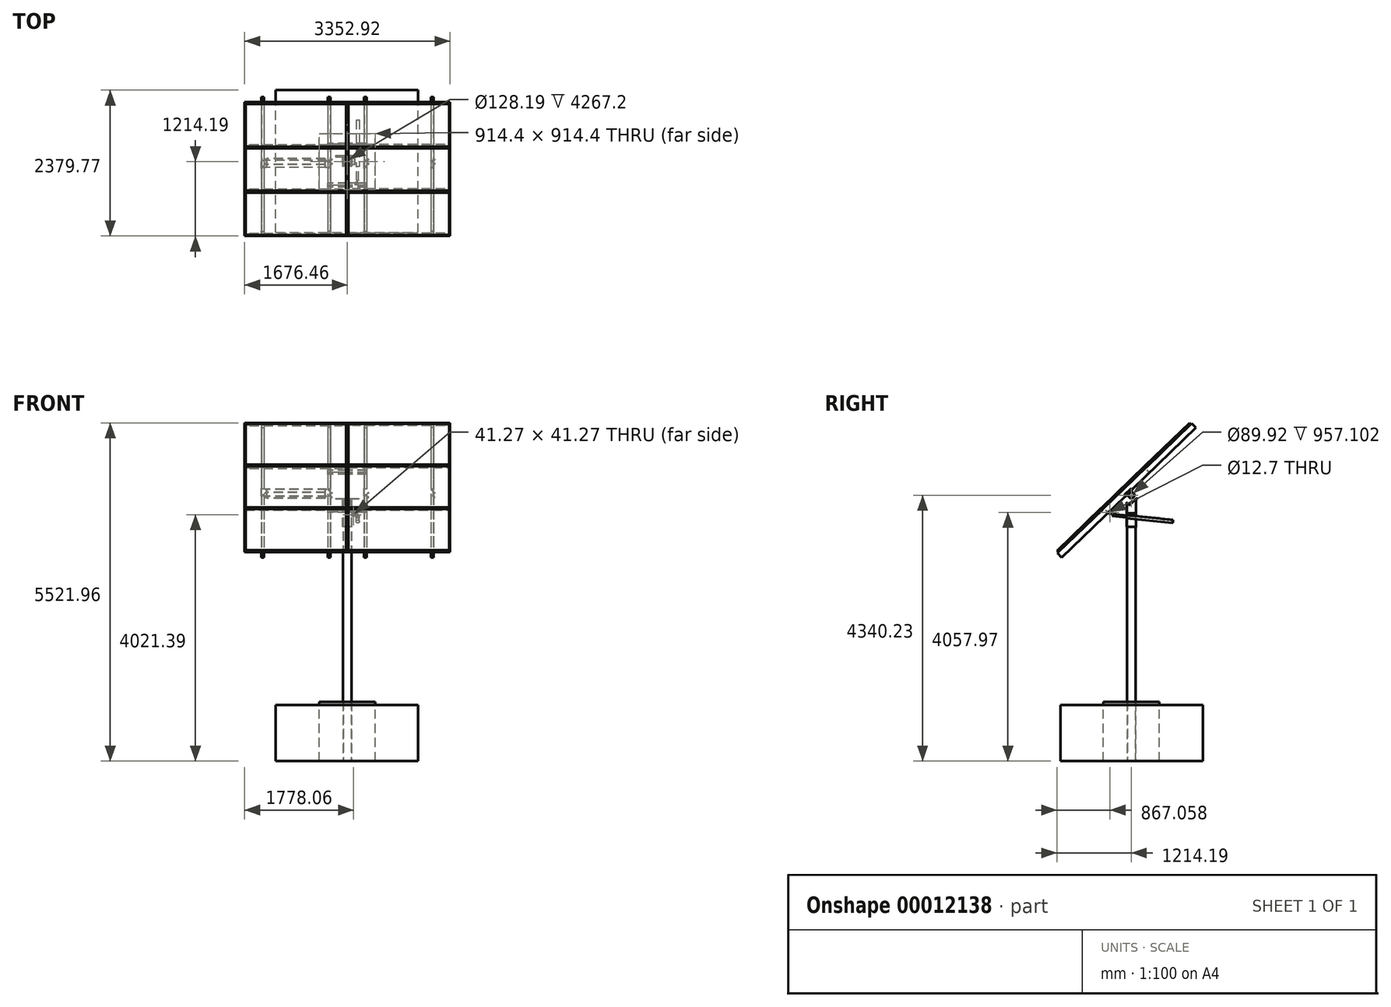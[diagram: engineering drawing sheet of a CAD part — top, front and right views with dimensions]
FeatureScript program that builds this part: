
annotation { "Feature Type Name" : "Feature", "Feature Type Description" : "" }
export const myFeature = defineFeature(function(context is Context, id is Id, definition is map)
    precondition{}
    {
        {
            var Q0;
            Q0=qCreatedBy(makeId("Top.planeOp"),FACE);
            var sketch = newSketch(context, id + "F0", { "sketchPlane" : qUnion([Q0])});
            skCircle(sketch, "E0", {"center": v(0, 0) * mm, "radius": 64.1 * mm});
            skCircle(sketch, "E1", {"center": v(0, 0) * mm, "radius": 70.65 * mm});
            skCircle(sketch, "E2", {"center": v(0, 0) * mm, "radius": 457.2 * mm, "construction": true});
            skLineSegment(sketch, "E3.bottom", {"start": v(-1167.5, -1157.81) * mm, "end": v(1155.89, -1157.81) * mm});
            skLineSegment(sketch, "E3.top", {"start": v(-1167.5, 1165.58) * mm, "end": v(1155.89, 1165.58) * mm});
            skLineSegment(sketch, "E3.left", {"start": v(-1167.5, -1157.81) * mm, "end": v(-1167.5, 1165.58) * mm});
            skLineSegment(sketch, "E3.right", {"start": v(1155.89, -1157.81) * mm, "end": v(1155.89, 1165.58) * mm});
            skLineSegment(sketch, "E4", {"start": v(0, 1165.58) * mm, "end": v(0, -1157.81) * mm, "construction": true});
            skLineSegment(sketch, "E5", {"start": v(-1167.5, 0) * mm, "end": v(1155.89, 0) * mm, "construction": true});
            skLineSegment(sketch, "E6.bottom", {"start": v(-457.2, -457.2) * mm, "end": v(457.2, -457.2) * mm});
            skLineSegment(sketch, "E6.top", {"start": v(-457.2, 457.2) * mm, "end": v(457.2, 457.2) * mm});
            skLineSegment(sketch, "E6.left", {"start": v(-457.2, -457.2) * mm, "end": v(-457.2, 457.2) * mm});
            skLineSegment(sketch, "E6.right", {"start": v(457.2, -457.2) * mm, "end": v(457.2, 457.2) * mm});
            skSolve(sketch);
        }
        {
            var Q0;
            Q0=makeQuery(id+"F0.imprint","IMPRINT",FACE,{"disambiguationData":[TD([[makeQuery(id+"F0.imprint","IMPRINT",EDGE,{"derivedFrom":sQuery(id+"F0.wireOp",EDGE,"E1")}),-1.0]])]});
            var Q1;
            Q1=makeQuery(id+"F0.imprint","IMPRINT",FACE,{"disambiguationData":[TD([[makeQuery(id+"F0.imprint","IMPRINT",EDGE,{"derivedFrom":sQuery(id+"F0.wireOp",EDGE,"E0")}),1.0]])]});
            var Q2;
            Q2=makeQuery(id+"F0.imprint","IMPRINT",FACE,{"disambiguationData":[TD([[makeQuery(id+"F0.imprint","IMPRINT",EDGE,{"derivedFrom":sQuery(id+"F0.wireOp",EDGE,"E0")}),-1.0]])]});
            extrude(context, id + "F1", {"entities" : qUnion([Q0, Q1, Q2]), "oppositeDirection" : true, "depth" : 914.4 * mm, "hasSecondDirection" : true, "secondDirectionOppositeDirection" : false, "secondDirectionDepth" : 50.8 * mm});
        }
        {
            var Q0;
            Q0=makeQuery(id+"F0.imprint","IMPRINT",FACE,{"disambiguationData":[TD([[makeQuery(id+"F0.imprint","IMPRINT",EDGE,{"derivedFrom":sQuery(id+"F0.wireOp",EDGE,"E0")}),-1.0]])]});
            extrude(context, id + "F2", {"entities" : qUnion([Q0]), "depth" : 3352.8 * mm, "hasSecondDirection" : true, "secondDirectionOppositeDirection" : true, "secondDirectionDepth" : 914.4 * mm});
        }
        {
            var Q0;
            Q0=makeQuery(id+"F0.imprint","IMPRINT",FACE,{"disambiguationData":[TD([[makeQuery(id+"F0.imprint","IMPRINT",EDGE,{"derivedFrom":sQuery(id+"F0.wireOp",EDGE,"E3.bottom")}),1.0]])]});
            extrude(context, id + "F3", {"entities" : qUnion([Q0]), "oppositeDirection" : true, "depth" : 914.4 * mm});
        }
        {
            var Q0;
            Q0=makeQuery(id+"F2.opExtrude","CAP_FACE",FACE,{"disambiguationData":[OSD([sQuery(id+"F0.wireOp",EDGE,"E0"),sQuery(id+"F0.wireOp",EDGE,"E1")])],"isStart":false});
            var sketch = newSketch(context, id + "F4", { "sketchPlane" : qUnion([Q0])});
            skCircle(sketch, "E7.0", {"center": v(0, 0) * mm, "radius": 70.65 * mm});
            skCircle(sketch, "E8", {"center": v(0, 49.5) * mm, "radius": 12.7 * mm});
            skCircle(sketch, "E9", {"center": v(0, 49.5) * mm, "radius": 6.35 * mm});
            skCircle(sketch, "E10", {"center": v(0, 49.5) * mm, "radius": 14.6 * mm, "construction": true});
            skLineSegment(sketch, "E11", {"start": v(0, 49.5) * mm, "end": v(0, 0) * mm, "construction": true});
            skCircle(sketch, "E12.1.0", {"center": v(-42.86, -24.75) * mm, "radius": 12.7 * mm});
            skCircle(sketch, "E12.1.1", {"center": v(-42.86, -24.75) * mm, "radius": 6.35 * mm});
            skCircle(sketch, "E12.2.0", {"center": v(42.86, -24.75) * mm, "radius": 12.7 * mm});
            skCircle(sketch, "E12.2.1", {"center": v(42.86, -24.75) * mm, "radius": 6.35 * mm});
            skSolve(sketch);
        }
        {
            var Q0;
            Q0 = qSketchRegion(id + "F4", true);
            var Q1;
            Q1=makeQuery(id+"F4.imprint","IMPRINT",FACE,{"disambiguationData":[TD([[makeQuery(id+"F4.imprint","IMPRINT",EDGE,{"derivedFrom":sQuery(id+"F4.wireOp",EDGE,"E8")}),1.0]])]});
            var Q2;
            Q2=makeQuery(id+"F4.imprint","IMPRINT",FACE,{"disambiguationData":[TD([[makeQuery(id+"F4.imprint","IMPRINT",EDGE,{"derivedFrom":sQuery(id+"F4.wireOp",EDGE,"E9")}),1.0]])]});
            var Q3;
            Q3=makeQuery(id+"F4.imprint","IMPRINT",FACE,{"disambiguationData":[TD([[makeQuery(id+"F4.imprint","IMPRINT",EDGE,{"derivedFrom":sQuery(id+"F4.wireOp",EDGE,"E12.1.0")}),1.0]])]});
            var Q4;
            Q4=makeQuery(id+"F4.imprint","IMPRINT",FACE,{"disambiguationData":[TD([[makeQuery(id+"F4.imprint","IMPRINT",EDGE,{"derivedFrom":sQuery(id+"F4.wireOp",EDGE,"E12.1.1")}),1.0]])]});
            var Q5;
            Q5=makeQuery(id+"F4.imprint","IMPRINT",FACE,{"disambiguationData":[TD([[makeQuery(id+"F4.imprint","IMPRINT",EDGE,{"derivedFrom":sQuery(id+"F4.wireOp",EDGE,"E12.2.1")}),1.0]])]});
            var Q6;
            Q6=makeQuery(id+"F4.imprint","IMPRINT",FACE,{"disambiguationData":[TD([[makeQuery(id+"F4.imprint","IMPRINT",EDGE,{"derivedFrom":sQuery(id+"F4.wireOp",EDGE,"E12.2.0")}),1.0]])]});
            extrude(context, id + "F5", {"entities" : qUnion([Q0, Q1, Q2, Q3, Q4, Q5, Q6]), "depth" : 6.35 * mm});
        }
        {
            var Q0;
            Q0=makeQuery(id+"F4.imprint","IMPRINT",FACE,{"disambiguationData":[TD([[makeQuery(id+"F4.imprint","IMPRINT",EDGE,{"derivedFrom":sQuery(id+"F4.wireOp",EDGE,"E8")}),1.0]])]});
            var Q1;
            Q1=makeQuery(id+"F4.imprint","IMPRINT",FACE,{"disambiguationData":[TD([[makeQuery(id+"F4.imprint","IMPRINT",EDGE,{"derivedFrom":sQuery(id+"F4.wireOp",EDGE,"E12.1.0")}),1.0]])]});
            var Q2;
            Q2=makeQuery(id+"F4.imprint","IMPRINT",FACE,{"disambiguationData":[TD([[makeQuery(id+"F4.imprint","IMPRINT",EDGE,{"derivedFrom":sQuery(id+"F4.wireOp",EDGE,"E12.2.0")}),1.0]])]});
            extrude(context, id + "F6", {"entities" : qUnion([Q0, Q1, Q2]), "oppositeDirection" : true, "depth" : 3.8 * mm});
        }
        {
            var Q0;
            Q0=makeQuery(id+"F5.opExtrude","CAP_FACE",FACE,{"disambiguationData":[OSD([sQuery(id+"F4.wireOp",EDGE,"E7.0")])],"isStart":false});
            var sketch = newSketch(context, id + "F7", { "sketchPlane" : qUnion([Q0])});
            skCircle(sketch, "E13", {"center": v(0, 0) * mm, "radius": 67.48 * mm});
            skCircle(sketch, "E14.0", {"center": v(0, 0) * mm, "radius": 70.65 * mm, "construction": true});
            skSolve(sketch);
        }
        {
            var Q0;
            Q0=makeQuery(id+"F7.imprint","IMPRINT",FACE,{"disambiguationData":[TD([[makeQuery(id+"F7.imprint","IMPRINT",EDGE,{"derivedFrom":sQuery(id+"F7.wireOp",EDGE,"E13")}),1.0]])]});
            extrude(context, id + "F8", {"entities" : qUnion([Q0]), "operationType" : NewBodyOperationType.ADD, "depth" : 6.35 * mm});
        }
        {
            var Q0;
            Q0=makeQuery(id+"F8.opExtrude","CAP_FACE",FACE,{"disambiguationData":[OSD([sQuery(id+"F7.wireOp",EDGE,"E13")])],"isStart":false});
            var sketch = newSketch(context, id + "F9", { "sketchPlane" : qUnion([Q0])});
            skCircle(sketch, "E15", {"center": v(0, 0) * mm, "radius": 84.14 * mm, "construction": true});
            skCircle(sketch, "E16", {"center": v(0, 0) * mm, "radius": 77.03 * mm, "construction": true});
            skLineSegment(sketch, "E17.rect.bottom", {"start": v(63.5, 76.2) * mm, "end": v(-63.5, 76.2) * mm});
            skLineSegment(sketch, "E17.rect.top", {"start": v(63.5, -76.2) * mm, "end": v(-63.5, -76.2) * mm});
            skLineSegment(sketch, "E17.rect.left", {"start": v(76.2, 63.5) * mm, "end": v(76.2, -63.5) * mm});
            skLineSegment(sketch, "E17.rect.right", {"start": v(-76.2, 63.5) * mm, "end": v(-76.2, -63.5) * mm});
            skPoint(sketch, "E18.visualSharp", {"position": v(-76.2, 76.2) * mm});
            skArc(sketch, "E18.filletArc", {"start": v(-63.5, 76.2) * mm, "mid": v(-72.48, 72.48) * mm, "end": v(-76.2, 63.5) * mm});
            skPoint(sketch, "E19.visualSharp", {"position": v(76.2, 76.2) * mm});
            skArc(sketch, "E19.filletArc", {"start": v(76.2, 63.5) * mm, "mid": v(72.48, 72.48) * mm, "end": v(63.5, 76.2) * mm});
            skPoint(sketch, "E20.visualSharp", {"position": v(76.2, -76.2) * mm});
            skArc(sketch, "E20.filletArc", {"start": v(63.5, -76.2) * mm, "mid": v(72.48, -72.48) * mm, "end": v(76.2, -63.5) * mm});
            skPoint(sketch, "E21.visualSharp", {"position": v(-76.2, -76.2) * mm});
            skArc(sketch, "E21.filletArc", {"start": v(-76.2, -63.5) * mm, "mid": v(-72.48, -72.48) * mm, "end": v(-63.5, -76.2) * mm});
            skArc(sketch, "E22.0", {"start": v(71.44, 63.5) * mm, "mid": v(69.11, 69.11) * mm, "end": v(63.5, 71.44) * mm});
            skLineSegment(sketch, "E22.1", {"start": v(71.44, 63.5) * mm, "end": v(71.44, -63.5) * mm});
            skArc(sketch, "E22.2", {"start": v(63.5, -71.44) * mm, "mid": v(69.11, -69.11) * mm, "end": v(71.44, -63.5) * mm});
            skLineSegment(sketch, "E22.3", {"start": v(63.5, -71.44) * mm, "end": v(-63.5, -71.44) * mm});
            skArc(sketch, "E22.4", {"start": v(-71.44, -63.5) * mm, "mid": v(-69.11, -69.11) * mm, "end": v(-63.5, -71.44) * mm});
            skLineSegment(sketch, "E22.5", {"start": v(63.5, 71.44) * mm, "end": v(-63.5, 71.44) * mm});
            skLineSegment(sketch, "E22.6", {"start": v(-71.44, 63.5) * mm, "end": v(-71.44, -63.5) * mm});
            skArc(sketch, "E22.7", {"start": v(-63.5, 71.44) * mm, "mid": v(-69.11, 69.11) * mm, "end": v(-71.44, 63.5) * mm});
            skSolve(sketch);
        }
        {
            var Q0;
            Q0=makeQuery(id+"F9.imprint","IMPRINT",FACE,{"disambiguationData":[TD([[makeQuery(id+"F9.imprint","IMPRINT",EDGE,{"derivedFrom":sQuery(id+"F9.wireOp",EDGE,"E17.rect.bottom")}),1.0]])]});
            extrude(context, id + "F10", {"entities" : qUnion([Q0]), "oppositeDirection" : true, "depth" : 457.2 * mm});
        }
        {
            var Q0;
            Q0=makeQuery(id+"F8.opExtrude","CAP_FACE",FACE,{"disambiguationData":[OSD([sQuery(id+"F7.wireOp",EDGE,"E13")])],"isStart":false});
            var sketch = newSketch(context, id + "F11", { "sketchPlane" : qUnion([Q0])});
            skLineSegment(sketch, "E23.bottom", {"start": v(-190.5, 99.71) * mm, "end": v(190.5, 99.71) * mm});
            skLineSegment(sketch, "E23.top", {"start": v(-190.5, -99.71) * mm, "end": v(190.5, -99.71) * mm});
            skLineSegment(sketch, "E23.left", {"start": v(-190.5, 99.71) * mm, "end": v(-190.5, -99.71) * mm});
            skLineSegment(sketch, "E23.right", {"start": v(190.5, 99.71) * mm, "end": v(190.5, -99.71) * mm});
            skLineSegment(sketch, "E24", {"start": v(0, 0) * mm, "end": v(0, 99.71) * mm, "construction": true});
            skLineSegment(sketch, "E25", {"start": v(0, 0) * mm, "end": v(190.5, 0) * mm, "construction": true});
            skLineSegment(sketch, "E26", {"start": v(84.14, 0) * mm, "end": v(84.14, 86.97) * mm, "construction": true});
            skCircle(sketch, "E27", {"center": v(-165.1, 58.74) * mm, "radius": 7.94 * mm});
            skCircle(sketch, "E28", {"center": v(-101.6, 58.74) * mm, "radius": 7.94 * mm});
            skLineSegment(sketch, "E29", {"start": v(-165.1, 58.74) * mm, "end": v(-101.6, 58.74) * mm, "construction": true});
            skCircle(sketch, "E30.0.MirrorC", {"center": v(-101.6, -58.74) * mm, "radius": 7.94 * mm});
            skCircle(sketch, "E30.1.MirrorC", {"center": v(-165.1, -58.74) * mm, "radius": 7.94 * mm});
            skCircle(sketch, "E31.0.MirrorC", {"center": v(165.1, -58.74) * mm, "radius": 7.94 * mm});
            skCircle(sketch, "E31.2.MirrorC", {"center": v(101.6, -58.74) * mm, "radius": 7.94 * mm});
            skCircle(sketch, "E31.3.MirrorC", {"center": v(101.6, 58.74) * mm, "radius": 7.94 * mm});
            skCircle(sketch, "E31.4.MirrorC", {"center": v(165.1, 58.74) * mm, "radius": 7.94 * mm});
            skLineSegment(sketch, "E32", {"start": v(-190.5, 50.8) * mm, "end": v(190.5, 50.8) * mm, "construction": true});
            skCircle(sketch, "E33", {"center": v(-165.1, 58.74) * mm, "radius": 25.4 * mm, "construction": true});
            skCircle(sketch, "E34", {"center": v(0, 0) * mm, "radius": 99.71 * mm, "construction": true});
            skCircle(sketch, "E35", {"center": v(-101.6, 58.74) * mm, "radius": 25.4 * mm, "construction": true});
            skSolve(sketch);
        }
        {
            var Q0;
            Q0=makeQuery(id+"F11.imprint","IMPRINT",FACE,{"disambiguationData":[TD([[makeQuery(id+"F11.imprint","IMPRINT",EDGE,{"derivedFrom":makeQuery(id+"F9.imprint","IMPRINT",EDGE,{"derivedFrom":sQuery(id+"F9.wireOp",EDGE,"E16")})}),1.0]])]});
            var Q1;
            Q1=makeQuery(id+"F11.imprint","IMPRINT",FACE,{"disambiguationData":[TD([[makeQuery(id+"F11.imprint","IMPRINT",EDGE,{"derivedFrom":makeQuery(id+"F9.imprint","IMPRINT",EDGE,{"derivedFrom":sQuery(id+"F9.wireOp",EDGE,"E15")})}),1.0]])]});
            var Q2;
            Q2=makeQuery(id+"F11.imprint","IMPRINT",FACE,{"disambiguationData":[TD([[makeQuery(id+"F11.imprint","IMPRINT",EDGE,{"derivedFrom":makeQuery(id+"F8.opExtrude","CAP_EDGE",EDGE,{"disambiguationData":[OSD([sQuery(id+"F7.wireOp",EDGE,"E13")])],"isStart":false})}),1.0]])]});
            var Q3;
            Q3=makeQuery(id+"F11.imprint","IMPRINT",FACE,{"disambiguationData":[TD([[makeQuery(id+"F11.imprint","IMPRINT",EDGE,{"derivedFrom":sQuery(id+"F11.wireOp",EDGE,"E23.bottom")}),-1.0]])]});
            extrude(context, id + "F12", {"entities" : qUnion([Q0, Q1, Q2, Q3]), "depth" : 6.35 * mm});
        }
        {
            var Q0;
            Q0=makeQuery(id+"F12.opExtrude","CAP_FACE",FACE,{"disambiguationData":[OSD([sQuery(id+"F11.wireOp",EDGE,"E23.bottom"),sQuery(id+"F11.wireOp",EDGE,"E23.top"),sQuery(id+"F11.wireOp",EDGE,"E23.left"),sQuery(id+"F11.wireOp",EDGE,"E23.right"),sQuery(id+"F11.wireOp",EDGE,"E27"),sQuery(id+"F11.wireOp",EDGE,"E28"),sQuery(id+"F11.wireOp",EDGE,"E30.0.MirrorC"),sQuery(id+"F11.wireOp",EDGE,"E30.1.MirrorC"),sQuery(id+"F11.wireOp",EDGE,"E31.0.MirrorC"),sQuery(id+"F11.wireOp",EDGE,"E31.2.MirrorC"),sQuery(id+"F11.wireOp",EDGE,"E31.3.MirrorC"),sQuery(id+"F11.wireOp",EDGE,"E31.4.MirrorC")])],"isStart":false});
            var sketch = newSketch(context, id + "F13", { "sketchPlane" : qUnion([Q0])});
            skLineSegment(sketch, "E36.bottom", {"start": v(-190.5, 25.4) * mm, "end": v(190.5, 25.4) * mm});
            skLineSegment(sketch, "E36.top", {"start": v(-190.5, -25.4) * mm, "end": v(190.5, -25.4) * mm});
            skLineSegment(sketch, "E36.left", {"start": v(-190.5, 25.4) * mm, "end": v(-190.5, -25.4) * mm});
            skLineSegment(sketch, "E36.right", {"start": v(190.5, 25.4) * mm, "end": v(190.5, -25.4) * mm});
            skLineSegment(sketch, "E37", {"start": v(-190.5, 0) * mm, "end": v(190.5, 0) * mm, "construction": true});
            skSolve(sketch);
        }
        {
            var Q0;
            Q0=makeQuery(id+"F13.imprint","IMPRINT",FACE,{"disambiguationData":[TD([[makeQuery(id+"F13.imprint","IMPRINT",EDGE,{"derivedFrom":sQuery(id+"F13.wireOp",EDGE,"E36.bottom")}),-1.0]])]});
            extrude(context, id + "F14", {"entities" : qUnion([Q0]), "depth" : 6.35 * mm});
        }
        {
            var Q0;
            Q0=qCreatedBy(makeId("Right.planeOp"),FACE);
            var sketch = newSketch(context, id + "F15", { "sketchPlane" : qUnion([Q0])});
            skCircle(sketch, "E38", {"center": v(0, 3425.83) * mm, "radius": 50.8 * mm});
            skCircle(sketch, "E39", {"center": v(0, 3425.83) * mm, "radius": 44.96 * mm});
            skLineSegment(sketch, "E40", {"start": v(0, 3375.03) * mm, "end": v(115.98, 3375.03) * mm, "construction": true});
            skLineSegment(sketch, "E41", {"start": v(0, 3425.83) * mm, "end": v(0, 0) * mm, "construction": true});
            skLineSegment(sketch, "E42", {"start": v(0, 3425.83) * mm, "end": v(0, 3476.63) * mm, "construction": true});
            skLineSegment(sketch, "E43", {"start": v(0, 3425.83) * mm, "end": v(-35.29, 3462.37) * mm, "construction": true});
            skLineSegment(sketch, "E44", {"start": v(-96.98, 3411.62) * mm, "end": v(17.58, 3522.25) * mm});
            skLineSegment(sketch, "E45", {"start": v(17.58, 3522.25) * mm, "end": v(22, 3517.68) * mm});
            skLineSegment(sketch, "E46", {"start": v(22, 3517.68) * mm, "end": v(-92.57, 3407.05) * mm});
            skLineSegment(sketch, "E47", {"start": v(-92.57, 3407.05) * mm, "end": v(-96.98, 3411.62) * mm});
            skPoint(sketch, "E48", {"position": v(-35.29, 3462.37) * mm});
            skLineSegment(sketch, "E49", {"start": v(-39.7, 3466.94) * mm, "end": v(-35.29, 3462.37) * mm, "construction": true});
            skLineSegment(sketch, "E50", {"start": v(-36.54, 3390.54) * mm, "end": v(0, 3425.83) * mm, "construction": true});
            skLineSegment(sketch, "E51", {"start": v(0, 3425.83) * mm, "end": v(36.54, 3461.11) * mm, "construction": true});
            skLineSegment(sketch, "E52", {"start": v(36.54, 3461.11) * mm, "end": v(48.14, 3472.32) * mm, "construction": true});
            skLineSegment(sketch, "E53", {"start": v(1.25, 3497.66) * mm, "end": v(22, 3517.68) * mm, "construction": true});
            skCircle(sketch, "E54", {"center": v(42.43, 3466.8) * mm, "radius": 8.2 * mm, "construction": true});
            skCircle(sketch, "E55", {"center": v(42.43, 3466.8) * mm, "radius": 7.94 * mm, "construction": true});
            skLineSegment(sketch, "E56", {"start": v(48.14, 3472.32) * mm, "end": v(21.98, 3499.42) * mm});
            skSolve(sketch);
        }
        {
            var Q0;
            Q0=makeQuery(id+"F15.imprint","IMPRINT",FACE,{"disambiguationData":[TD([[makeQuery(id+"F15.imprint","IMPRINT",EDGE,{"derivedFrom":sQuery(id+"F15.wireOp",EDGE,"E38")}),1.0]])]});
            extrude(context, id + "F16", {"entities" : qUnion([Q0]), "depth" : 1524 * mm, "hasSecondDirection" : true, "secondDirectionOppositeDirection" : true, "secondDirectionDepth" : 1524 * mm});
        }
        {
            var Q0;
            Q0=makeQuery(id+"F15.imprint","IMPRINT",FACE,{"disambiguationData":[TD([[makeQuery(id+"F15.imprint","IMPRINT",EDGE,{"derivedFrom":sQuery(id+"F15.wireOp",EDGE,"E44")}),-1.0]])]});
            extrude(context, id + "F17", {"entities" : qUnion([Q0]), "depth" : 1524 * mm, "hasSecondDirection" : true, "secondDirectionOppositeDirection" : true, "secondDirectionDepth" : 1524 * mm});
        }
        {
            var Q0;
            Q0=makeQuery(id+"F17.opExtrude","SWEPT_FACE",FACE,{"disambiguationData":[OSD([sQuery(id+"F15.wireOp",EDGE,"E44")])]});
            cPlane(context, id + "F18", {"entities" : qUnion([Q0]), "cplaneType" : CPlaneType.OFFSET, "offset" : 101.6 * mm, "width" : 152.4 * mm, "height" : 152.4 * mm});
        }
        {
            var Q0;
            Q0=qCreatedBy(id+"F18.planeOp",FACE);
            var sketch = newSketch(context, id + "F19", { "sketchPlane" : qUnion([Q0])});
            skLineSegment(sketch, "E57.bottom", {"start": v(-1676.46, 3884.47) * mm, "end": v(-1.59, 3884.47) * mm});
            skLineSegment(sketch, "E57.top", {"start": v(-1676.46, 2883.46) * mm, "end": v(-1.59, 2883.46) * mm});
            skLineSegment(sketch, "E57.left", {"start": v(-1676.46, 3884.47) * mm, "end": v(-1676.46, 2883.46) * mm});
            skLineSegment(sketch, "E57.right", {"start": v(-1.59, 3884.47) * mm, "end": v(-1.59, 2883.46) * mm});
            skLineSegment(sketch, "E58.bottom", {"start": v(1.59, 3884.47) * mm, "end": v(1676.46, 3884.47) * mm});
            skLineSegment(sketch, "E58.top", {"start": v(1.59, 2883.46) * mm, "end": v(1676.46, 2883.46) * mm});
            skLineSegment(sketch, "E58.left", {"start": v(1.59, 3884.47) * mm, "end": v(1.59, 2883.46) * mm});
            skLineSegment(sketch, "E58.right", {"start": v(1676.46, 3884.47) * mm, "end": v(1676.46, 2883.46) * mm});
            skLineSegment(sketch, "E59.bottom", {"start": v(-1676.46, 2880.29) * mm, "end": v(-1.59, 2880.29) * mm});
            skLineSegment(sketch, "E59.top", {"start": v(-1676.46, 1879.27) * mm, "end": v(-1.59, 1879.27) * mm});
            skLineSegment(sketch, "E59.left", {"start": v(-1676.46, 2880.29) * mm, "end": v(-1676.46, 1879.27) * mm});
            skLineSegment(sketch, "E59.right", {"start": v(-1.59, 2880.29) * mm, "end": v(-1.59, 1879.27) * mm});
            skLineSegment(sketch, "E60.bottom", {"start": v(1.59, 2880.29) * mm, "end": v(1676.46, 2880.29) * mm});
            skLineSegment(sketch, "E60.top", {"start": v(1.59, 1879.27) * mm, "end": v(1676.46, 1879.27) * mm});
            skLineSegment(sketch, "E60.left", {"start": v(1.59, 2880.29) * mm, "end": v(1.59, 1879.27) * mm});
            skLineSegment(sketch, "E60.right", {"start": v(1676.46, 2880.29) * mm, "end": v(1676.46, 1879.27) * mm});
            skLineSegment(sketch, "E61.bottom", {"start": v(-1676.46, 1876.1) * mm, "end": v(-1.59, 1876.1) * mm});
            skLineSegment(sketch, "E61.top", {"start": v(-1676.46, 875.08) * mm, "end": v(-1.59, 875.08) * mm});
            skLineSegment(sketch, "E61.left", {"start": v(-1676.46, 1876.1) * mm, "end": v(-1676.46, 875.08) * mm});
            skLineSegment(sketch, "E61.right", {"start": v(-1.59, 1876.1) * mm, "end": v(-1.59, 875.08) * mm});
            skLineSegment(sketch, "E62.bottom", {"start": v(1.59, 1876.1) * mm, "end": v(1676.46, 1876.1) * mm});
            skLineSegment(sketch, "E62.top", {"start": v(1.59, 875.08) * mm, "end": v(1676.46, 875.08) * mm});
            skLineSegment(sketch, "E62.left", {"start": v(1.59, 1876.1) * mm, "end": v(1.59, 875.08) * mm});
            skLineSegment(sketch, "E62.right", {"start": v(1676.46, 1876.1) * mm, "end": v(1676.46, 875.08) * mm});
            skLineSegment(sketch, "E63", {"start": v(-1.59, 3884.47) * mm, "end": v(1.59, 3884.47) * mm, "construction": true});
            skLineSegment(sketch, "E64", {"start": v(-1.59, 2880.29) * mm, "end": v(1.59, 2880.29) * mm, "construction": true});
            skLineSegment(sketch, "E65", {"start": v(-1.59, 1876.1) * mm, "end": v(1.59, 1876.1) * mm, "construction": true});
            skLineSegment(sketch, "E66", {"start": v(-1676.46, 2883.46) * mm, "end": v(-1676.46, 2880.29) * mm, "construction": true});
            skLineSegment(sketch, "E67", {"start": v(1676.46, 2880.29) * mm, "end": v(1676.46, 2883.46) * mm, "construction": true});
            skLineSegment(sketch, "E68", {"start": v(1676.46, 1876.1) * mm, "end": v(1676.46, 1879.27) * mm, "construction": true});
            skLineSegment(sketch, "E69", {"start": v(-1676.46, 1876.1) * mm, "end": v(-1676.46, 1879.27) * mm, "construction": true});
            skPoint(sketch, "E70", {"position": v(0, 3884.47) * mm});
            skPoint(sketch, "E71", {"position": v(1676.46, 2379.78) * mm});
            skLineSegment(sketch, "E72.0", {"start": v(-1661.22, 3869.23) * mm, "end": v(-16.83, 3869.23) * mm});
            skLineSegment(sketch, "E72.1", {"start": v(-1661.22, 3869.23) * mm, "end": v(-1661.22, 2898.7) * mm});
            skLineSegment(sketch, "E72.2", {"start": v(-1661.22, 2898.7) * mm, "end": v(-16.83, 2898.7) * mm});
            skLineSegment(sketch, "E72.3", {"start": v(-16.83, 3869.23) * mm, "end": v(-16.83, 2898.7) * mm});
            skLineSegment(sketch, "E73.0", {"start": v(16.83, 3869.23) * mm, "end": v(1661.22, 3869.23) * mm});
            skLineSegment(sketch, "E73.1", {"start": v(16.83, 3869.23) * mm, "end": v(16.83, 2898.7) * mm});
            skLineSegment(sketch, "E73.2", {"start": v(16.83, 2898.7) * mm, "end": v(1661.22, 2898.7) * mm});
            skLineSegment(sketch, "E73.3", {"start": v(1661.22, 3869.23) * mm, "end": v(1661.22, 2898.7) * mm});
            skLineSegment(sketch, "E74.0", {"start": v(-1661.22, 2865.05) * mm, "end": v(-1661.22, 1894.51) * mm});
            skLineSegment(sketch, "E74.1", {"start": v(-1661.22, 2865.05) * mm, "end": v(-16.83, 2865.05) * mm});
            skLineSegment(sketch, "E74.2", {"start": v(-16.83, 2865.05) * mm, "end": v(-16.83, 1894.51) * mm});
            skLineSegment(sketch, "E74.3", {"start": v(-1661.22, 1894.51) * mm, "end": v(-16.83, 1894.51) * mm});
            skLineSegment(sketch, "E75.0", {"start": v(1661.22, 2865.05) * mm, "end": v(1661.22, 1894.51) * mm});
            skLineSegment(sketch, "E75.1", {"start": v(16.83, 2865.05) * mm, "end": v(1661.22, 2865.05) * mm});
            skLineSegment(sketch, "E75.2", {"start": v(16.83, 2865.05) * mm, "end": v(16.83, 1894.51) * mm});
            skLineSegment(sketch, "E75.3", {"start": v(16.83, 1894.51) * mm, "end": v(1661.22, 1894.51) * mm});
            skLineSegment(sketch, "E76.0", {"start": v(1661.22, 1860.86) * mm, "end": v(1661.22, 890.32) * mm});
            skLineSegment(sketch, "E76.1", {"start": v(16.83, 1860.86) * mm, "end": v(1661.22, 1860.86) * mm});
            skLineSegment(sketch, "E76.2", {"start": v(16.83, 1860.86) * mm, "end": v(16.83, 890.32) * mm});
            skLineSegment(sketch, "E76.3", {"start": v(16.83, 890.32) * mm, "end": v(1661.22, 890.32) * mm});
            skLineSegment(sketch, "E77.0", {"start": v(-16.83, 1860.86) * mm, "end": v(-16.83, 890.32) * mm});
            skLineSegment(sketch, "E77.1", {"start": v(-1661.22, 1860.86) * mm, "end": v(-16.83, 1860.86) * mm});
            skLineSegment(sketch, "E77.2", {"start": v(-1661.22, 1860.86) * mm, "end": v(-1661.22, 890.32) * mm});
            skLineSegment(sketch, "E77.3", {"start": v(-1661.22, 890.32) * mm, "end": v(-16.83, 890.32) * mm});
            skLineSegment(sketch, "E78", {"start": v(-1661.22, 2379.78) * mm, "end": v(1661.22, 2379.78) * mm, "construction": true});
            skLineSegment(sketch, "E79", {"start": v(0, 1065.88) * mm, "end": v(0, 2379.78) * mm, "construction": true});
            skSolve(sketch);
        }
        {
            var Q0;
            Q0=sQuery(id+"F15.wireOp",EDGE,"E51");
            var Q1;
            Q1=sQuery(id+"F15.wireOp",VERTEX,"E51.start");
            cPlane(context, id + "F20", {"entities" : qUnion([Q0, Q1]), "cplaneType" : CPlaneType.LINE_POINT, "offset" : 152.4 * mm, "width" : 152.4 * mm, "height" : 152.4 * mm});
        }
        {
            var Q0;
            {var subQ10=sQuery(id+"F19.wireOp",EDGE,"E59.left");Q0=makeQuery(id+"F19.imprint","IMPRINT",FACE,{"disambiguationData":[TD([[makeQuery(id+"F19.imprint","IMPRINT",EDGE,{"derivedFrom":subQ10}),1.0]])]});}
            var Q1;
            {var subQ0=sQuery(id+"F25.wireOp",EDGE,"E140");var subQ1=makeQuery(id+"F26.opExtrude","SWEPT_EDGE",EDGE,{"disambiguationData":[OSD([subQ0,sQuery(id+"F25.wireOp",EDGE,"E141")])]});var subQ4=sQuery(id+"F19.wireOp",EDGE,"E59.bottom");var subQ5=makeQuery(id+"F19.imprint","INTERSECT",VERTEX,{"derivedFrom":[subQ1,subQ4]});Q1=makeQuery(id+"F19.imprint","IMPRINT",FACE,{"disambiguationData":[TD([[makeQuery(id+"F19.imprint","IMPRINT",EDGE,{"disambiguationData":[TD([[subQ5,-1.0]])],"derivedFrom":subQ4}),-1.0]])]});}
            var Q2;
            {var subQ8=sQuery(id+"F19.wireOp",EDGE,"E59.right");Q2=makeQuery(id+"F19.imprint","IMPRINT",FACE,{"disambiguationData":[TD([[makeQuery(id+"F19.imprint","IMPRINT",EDGE,{"derivedFrom":subQ8}),-1.0]])]});}
            var Q3;
            {var subQ0=sQuery(id+"F25.wireOp",EDGE,"E140");var subQ1=makeQuery(id+"F26.opExtrude","SWEPT_EDGE",EDGE,{"disambiguationData":[OSD([subQ0,sQuery(id+"F25.wireOp",EDGE,"E141")])]});var subQ4=sQuery(id+"F19.wireOp",EDGE,"E57.top");var subQ5=makeQuery(id+"F19.imprint","INTERSECT",VERTEX,{"derivedFrom":[subQ1,subQ4]});Q3=makeQuery(id+"F19.imprint","IMPRINT",FACE,{"disambiguationData":[TD([[makeQuery(id+"F19.imprint","IMPRINT",EDGE,{"disambiguationData":[TD([[subQ5,-1.0]])],"derivedFrom":subQ4}),1.0]])]});}
            var Q4;
            {var subQ0=sQuery(id+"F25.wireOp",EDGE,"E140");var subQ1=makeQuery(id+"F26.opExtrude","SWEPT_EDGE",EDGE,{"disambiguationData":[OSD([subQ0,sQuery(id+"F25.wireOp",EDGE,"E141")])]});var subQ4=sQuery(id+"F19.wireOp",EDGE,"E59.top");var subQ5=makeQuery(id+"F19.imprint","INTERSECT",VERTEX,{"derivedFrom":[subQ1,subQ4]});Q4=makeQuery(id+"F19.imprint","IMPRINT",FACE,{"disambiguationData":[TD([[makeQuery(id+"F19.imprint","IMPRINT",EDGE,{"disambiguationData":[TD([[subQ5,-1.0]])],"derivedFrom":subQ4}),1.0]])]});}
            var Q5;
            {var subQ8=sQuery(id+"F19.wireOp",EDGE,"E61.left");Q5=makeQuery(id+"F19.imprint","IMPRINT",FACE,{"disambiguationData":[TD([[makeQuery(id+"F19.imprint","IMPRINT",EDGE,{"derivedFrom":subQ8}),1.0]])]});}
            var Q6;
            {var subQ0=sQuery(id+"F25.wireOp",EDGE,"E140");var subQ1=makeQuery(id+"F26.opExtrude","SWEPT_EDGE",EDGE,{"disambiguationData":[OSD([subQ0,sQuery(id+"F25.wireOp",EDGE,"E141")])]});var subQ4=sQuery(id+"F19.wireOp",EDGE,"E61.bottom");var subQ5=makeQuery(id+"F19.imprint","INTERSECT",VERTEX,{"derivedFrom":[subQ1,subQ4]});Q6=makeQuery(id+"F19.imprint","IMPRINT",FACE,{"disambiguationData":[TD([[makeQuery(id+"F19.imprint","IMPRINT",EDGE,{"disambiguationData":[TD([[subQ5,-1.0]])],"derivedFrom":subQ4}),-1.0]])]});}
            var Q7;
            {var subQ10=sQuery(id+"F19.wireOp",EDGE,"E61.right");Q7=makeQuery(id+"F19.imprint","IMPRINT",FACE,{"disambiguationData":[TD([[makeQuery(id+"F19.imprint","IMPRINT",EDGE,{"derivedFrom":subQ10}),-1.0]])]});}
            var Q8;
            {var subQ0=sQuery(id+"F25.wireOp",EDGE,"E140");var subQ1=makeQuery(id+"F26.opExtrude","SWEPT_EDGE",EDGE,{"disambiguationData":[OSD([subQ0,sQuery(id+"F25.wireOp",EDGE,"E141")])]});var subQ4=sQuery(id+"F19.wireOp",EDGE,"E61.top");var subQ5=makeQuery(id+"F19.imprint","INTERSECT",VERTEX,{"derivedFrom":[subQ1,subQ4]});Q8=makeQuery(id+"F19.imprint","IMPRINT",FACE,{"disambiguationData":[TD([[makeQuery(id+"F19.imprint","IMPRINT",EDGE,{"disambiguationData":[TD([[subQ5,-1.0]])],"derivedFrom":subQ4}),1.0]])]});}
            var Q9;
            Q9=makeQuery(id+"F19.imprint","IMPRINT",FACE,{"disambiguationData":[TD([[makeQuery(id+"F19.imprint","IMPRINT",EDGE,{"derivedFrom":sQuery(id+"F19.wireOp",EDGE,"E62.bottom")}),-1.0]])]});
            var Q10;
            Q10=makeQuery(id+"F19.imprint","IMPRINT",FACE,{"disambiguationData":[TD([[makeQuery(id+"F19.imprint","IMPRINT",EDGE,{"derivedFrom":sQuery(id+"F19.wireOp",EDGE,"E60.bottom")}),-1.0]])]});
            var Q11;
            Q11=makeQuery(id+"F19.imprint","IMPRINT",FACE,{"disambiguationData":[TD([[makeQuery(id+"F19.imprint","IMPRINT",EDGE,{"derivedFrom":sQuery(id+"F19.wireOp",EDGE,"E58.bottom")}),-1.0]])]});
            var Q12;
            {var subQ0=sQuery(id+"F25.wireOp",EDGE,"E140");var subQ1=makeQuery(id+"F26.opExtrude","SWEPT_EDGE",EDGE,{"disambiguationData":[OSD([subQ0,sQuery(id+"F25.wireOp",EDGE,"E141")])]});var subQ4=sQuery(id+"F19.wireOp",EDGE,"E57.bottom");var subQ5=makeQuery(id+"F19.imprint","INTERSECT",VERTEX,{"derivedFrom":[subQ1,subQ4]});Q12=makeQuery(id+"F19.imprint","IMPRINT",FACE,{"disambiguationData":[TD([[makeQuery(id+"F19.imprint","IMPRINT",EDGE,{"disambiguationData":[TD([[subQ5,-1.0]])],"derivedFrom":subQ4}),-1.0]])]});}
            var Q13;
            {var subQ10=sQuery(id+"F19.wireOp",EDGE,"E57.right");Q13=makeQuery(id+"F19.imprint","IMPRINT",FACE,{"disambiguationData":[TD([[makeQuery(id+"F19.imprint","IMPRINT",EDGE,{"derivedFrom":subQ10}),-1.0]])]});}
            var Q14;
            {var subQ10=sQuery(id+"F19.wireOp",EDGE,"E57.left");Q14=makeQuery(id+"F19.imprint","IMPRINT",FACE,{"disambiguationData":[TD([[makeQuery(id+"F19.imprint","IMPRINT",EDGE,{"derivedFrom":subQ10}),1.0]])]});}
            extrude(context, id + "F21", {"entities" : qUnion([Q0, Q1, Q2, Q3, Q4, Q5, Q6, Q7, Q8, Q9, Q10, Q11, Q12, Q13, Q14]), "depth" : 30.99 * mm});
        }
        {
            var Q0;
            {var subQ5=sQuery(id+"F19.wireOp",EDGE,"E72.3");Q0=makeQuery(id+"F19.imprint","IMPRINT",FACE,{"disambiguationData":[TD([[makeQuery(id+"F19.imprint","IMPRINT",EDGE,{"derivedFrom":subQ5}),-1.0]])]});}
            var Q1;
            {var subQ5=sQuery(id+"F19.wireOp",EDGE,"E72.1");Q1=makeQuery(id+"F19.imprint","IMPRINT",FACE,{"disambiguationData":[TD([[makeQuery(id+"F19.imprint","IMPRINT",EDGE,{"derivedFrom":subQ5}),1.0]])]});}
            var Q2;
            {var subQ0=sQuery(id+"F25.wireOp",EDGE,"E140");var subQ1=makeQuery(id+"F26.opExtrude","SWEPT_EDGE",EDGE,{"disambiguationData":[OSD([subQ0,sQuery(id+"F25.wireOp",EDGE,"E141")])]});var subQ4=sQuery(id+"F19.wireOp",EDGE,"E72.0");var subQ5=makeQuery(id+"F19.imprint","INTERSECT",VERTEX,{"derivedFrom":[subQ1,subQ4]});Q2=makeQuery(id+"F19.imprint","IMPRINT",FACE,{"disambiguationData":[TD([[makeQuery(id+"F19.imprint","IMPRINT",EDGE,{"disambiguationData":[TD([[subQ5,-1.0]])],"derivedFrom":subQ4}),-1.0]])]});}
            var Q3;
            Q3=makeQuery(id+"F19.imprint","IMPRINT",FACE,{"disambiguationData":[TD([[makeQuery(id+"F19.imprint","IMPRINT",EDGE,{"derivedFrom":sQuery(id+"F19.wireOp",EDGE,"E73.0")}),-1.0]])]});
            var Q4;
            Q4=makeQuery(id+"F19.imprint","IMPRINT",FACE,{"disambiguationData":[TD([[makeQuery(id+"F19.imprint","IMPRINT",EDGE,{"derivedFrom":sQuery(id+"F19.wireOp",EDGE,"E75.0")}),-1.0]])]});
            var Q5;
            {var subQ5=sQuery(id+"F19.wireOp",EDGE,"E74.2");Q5=makeQuery(id+"F19.imprint","IMPRINT",FACE,{"disambiguationData":[TD([[makeQuery(id+"F19.imprint","IMPRINT",EDGE,{"derivedFrom":subQ5}),-1.0]])]});}
            var Q6;
            {var subQ5=sQuery(id+"F19.wireOp",EDGE,"E77.0");Q6=makeQuery(id+"F19.imprint","IMPRINT",FACE,{"disambiguationData":[TD([[makeQuery(id+"F19.imprint","IMPRINT",EDGE,{"derivedFrom":subQ5}),-1.0]])]});}
            var Q7;
            {var subQ5=sQuery(id+"F19.wireOp",EDGE,"E74.0");Q7=makeQuery(id+"F19.imprint","IMPRINT",FACE,{"disambiguationData":[TD([[makeQuery(id+"F19.imprint","IMPRINT",EDGE,{"derivedFrom":subQ5}),1.0]])]});}
            var Q8;
            {var subQ5=sQuery(id+"F19.wireOp",EDGE,"E77.2");Q8=makeQuery(id+"F19.imprint","IMPRINT",FACE,{"disambiguationData":[TD([[makeQuery(id+"F19.imprint","IMPRINT",EDGE,{"derivedFrom":subQ5}),1.0]])]});}
            var Q9;
            {var subQ0=sQuery(id+"F25.wireOp",EDGE,"E140");var subQ1=makeQuery(id+"F26.opExtrude","SWEPT_EDGE",EDGE,{"disambiguationData":[OSD([subQ0,sQuery(id+"F25.wireOp",EDGE,"E141")])]});var subQ4=sQuery(id+"F19.wireOp",EDGE,"E74.1");var subQ5=makeQuery(id+"F19.imprint","INTERSECT",VERTEX,{"derivedFrom":[subQ1,subQ4]});Q9=makeQuery(id+"F19.imprint","IMPRINT",FACE,{"disambiguationData":[TD([[makeQuery(id+"F19.imprint","IMPRINT",EDGE,{"disambiguationData":[TD([[subQ5,-1.0]])],"derivedFrom":subQ4}),-1.0]])]});}
            var Q10;
            Q10=makeQuery(id+"F19.imprint","IMPRINT",FACE,{"disambiguationData":[TD([[makeQuery(id+"F19.imprint","IMPRINT",EDGE,{"derivedFrom":sQuery(id+"F19.wireOp",EDGE,"E76.0")}),-1.0]])]});
            var Q11;
            {var subQ0=sQuery(id+"F25.wireOp",EDGE,"E140");var subQ1=makeQuery(id+"F26.opExtrude","SWEPT_EDGE",EDGE,{"disambiguationData":[OSD([subQ0,sQuery(id+"F25.wireOp",EDGE,"E141")])]});var subQ4=sQuery(id+"F19.wireOp",EDGE,"E77.1");var subQ5=makeQuery(id+"F19.imprint","INTERSECT",VERTEX,{"derivedFrom":[subQ1,subQ4]});Q11=makeQuery(id+"F19.imprint","IMPRINT",FACE,{"disambiguationData":[TD([[makeQuery(id+"F19.imprint","IMPRINT",EDGE,{"disambiguationData":[TD([[subQ5,-1.0]])],"derivedFrom":subQ4}),-1.0]])]});}
            extrude(context, id + "F22", {"entities" : qUnion([Q0, Q1, Q2, Q3, Q4, Q5, Q6, Q7, Q8, Q9, Q10, Q11]), "operationType" : NewBodyOperationType.ADD, "depth" : 27.94 * mm, "hasSecondDirection" : true, "secondDirectionOppositeDirection" : false, "secondDirectionDepth" : 21.59 * mm});
        }
        {
            var Q0;
            Q0=makeQuery(id+"F21.opExtrude","CAP_FACE",FACE,{"disambiguationData":[OSD([sQuery(id+"F19.wireOp",EDGE,"E61.bottom"),sQuery(id+"F19.wireOp",EDGE,"E61.top"),sQuery(id+"F19.wireOp",EDGE,"E61.left"),sQuery(id+"F19.wireOp",EDGE,"E61.right"),sQuery(id+"F19.wireOp",EDGE,"E77.0"),sQuery(id+"F19.wireOp",EDGE,"E77.1"),sQuery(id+"F19.wireOp",EDGE,"E77.2"),sQuery(id+"F19.wireOp",EDGE,"E77.3")])],"isStart":true});
            var sketch = newSketch(context, id + "F23", { "sketchPlane" : qUnion([Q0])});
            skLineSegment(sketch, "E80", {"start": v(-1592.64, -890.32) * mm, "end": v(-1592.64, -909.12) * mm});
            skLineSegment(sketch, "E81", {"start": v(-1592.64, -909.12) * mm, "end": v(-839.03, -909.12) * mm});
            skLineSegment(sketch, "E82", {"start": v(-839.03, -909.12) * mm, "end": v(-85.4, -909.12) * mm});
            skLineSegment(sketch, "E83", {"start": v(-85.4, -909.12) * mm, "end": v(-85.4, -890.32) * mm});
            skLineSegment(sketch, "E84", {"start": v(-85.4, -890.32) * mm, "end": v(-1592.64, -890.32) * mm});
            skLineSegment(sketch, "E85", {"start": v(-1661.22, -1375.59) * mm, "end": v(-16.83, -1375.59) * mm, "construction": true});
            skLineSegment(sketch, "E86", {"start": v(-1676.46, -1876.1) * mm, "end": v(-1676.46, -1879.27) * mm, "construction": true});
            skLineSegment(sketch, "E87", {"start": v(-2376, -1877.68) * mm, "end": v(-1676.46, -1877.68) * mm, "construction": true});
            skLineSegment(sketch, "E88", {"start": v(-1.59, -875.08) * mm, "end": v(1.59, -875.08) * mm, "construction": true});
            skLineSegment(sketch, "E89", {"start": v(0, -875.08) * mm, "end": v(0, 1965.98) * mm, "construction": true});
            skLineSegment(sketch, "E90", {"start": v(-839.03, -909.12) * mm, "end": v(-839.03, -1375.59) * mm, "construction": true});
            skLineSegment(sketch, "E91", {"start": v(-1661.22, -890.32) * mm, "end": v(-1676.46, -890.32) * mm, "construction": true});
            skLineSegment(sketch, "E92", {"start": v(-1668.84, 915.56) * mm, "end": v(-1668.84, -890.32) * mm, "construction": true});
            skLineSegment(sketch, "E93", {"start": v(-1592.64, -899.72) * mm, "end": v(-85.4, -899.72) * mm, "construction": true});
            skCircle(sketch, "E94", {"center": v(-1561.66, -899.72) * mm, "radius": 3.56 * mm});
            skCircle(sketch, "E95", {"center": v(-1381.06, -899.72) * mm, "radius": 4.76 * mm});
            skCircle(sketch, "E96.0.MirrorC", {"center": v(-296.99, -899.72) * mm, "radius": 4.76 * mm});
            skCircle(sketch, "E97.0.MirrorC", {"center": v(-1381.06, -1851.46) * mm, "radius": 4.76 * mm});
            skCircle(sketch, "E97.1.MirrorC", {"center": v(-1561.66, -1851.46) * mm, "radius": 3.56 * mm});
            skLineSegment(sketch, "E97.2.MirrorCS", {"start": v(-1592.64, -1842.06) * mm, "end": v(-839.03, -1842.06) * mm});
            skLineSegment(sketch, "E97.3.MirrorCS", {"start": v(-1592.64, -1860.86) * mm, "end": v(-1592.64, -1842.06) * mm});
            skLineSegment(sketch, "E97.4.MirrorCS", {"start": v(-839.03, -1842.06) * mm, "end": v(-85.4, -1842.06) * mm});
            skCircle(sketch, "E97.5.MirrorC", {"center": v(-296.99, -1851.46) * mm, "radius": 4.76 * mm});
            skLineSegment(sketch, "E97.6.MirrorCS", {"start": v(-85.4, -1842.06) * mm, "end": v(-85.4, -1860.86) * mm});
            skLineSegment(sketch, "E97.7.MirrorCS", {"start": v(-85.4, -1860.86) * mm, "end": v(-1592.64, -1860.86) * mm});
            skLineSegment(sketch, "E98.0.MirrorCS", {"start": v(-1592.64, -1913.3) * mm, "end": v(-839.03, -1913.3) * mm});
            skLineSegment(sketch, "E99.0.MirrorCS", {"start": v(-839.03, -1913.3) * mm, "end": v(-85.4, -1913.3) * mm});
            skLineSegment(sketch, "E100.0.MirrorCS", {"start": v(-1592.64, -1894.51) * mm, "end": v(-1592.64, -1913.3) * mm});
            skLineSegment(sketch, "E101.0.MirrorCS", {"start": v(-85.4, -1894.51) * mm, "end": v(-1592.64, -1894.51) * mm});
            skCircle(sketch, "E102.0.MirrorC", {"center": v(-1561.66, -1903.9) * mm, "radius": 3.56 * mm});
            skCircle(sketch, "E103.0.MirrorC", {"center": v(-1381.06, -1903.9) * mm, "radius": 4.76 * mm});
            skCircle(sketch, "E104.0.MirrorC", {"center": v(-296.99, -1903.9) * mm, "radius": 4.76 * mm});
            skLineSegment(sketch, "E105.0.MirrorCS", {"start": v(-85.4, -1913.3) * mm, "end": v(-85.4, -1894.51) * mm});
            skLineSegment(sketch, "E106.0.MirrorCS", {"start": v(-85.4, -2846.25) * mm, "end": v(-85.4, -2865.05) * mm});
            skLineSegment(sketch, "E107.0.MirrorCS", {"start": v(-839.03, -2846.25) * mm, "end": v(-85.4, -2846.25) * mm});
            skLineSegment(sketch, "E108.0.MirrorCS", {"start": v(-85.4, -2865.05) * mm, "end": v(-1592.64, -2865.05) * mm});
            skLineSegment(sketch, "E109.0.MirrorCS", {"start": v(-1592.64, -2865.05) * mm, "end": v(-1592.64, -2846.25) * mm});
            skCircle(sketch, "E110.0.MirrorC", {"center": v(-1561.66, -2855.65) * mm, "radius": 3.56 * mm});
            skCircle(sketch, "E111.0.MirrorC", {"center": v(-1381.06, -2855.65) * mm, "radius": 4.76 * mm});
            skLineSegment(sketch, "E112.0.MirrorCS", {"start": v(-1592.64, -2846.25) * mm, "end": v(-839.03, -2846.25) * mm});
            skLineSegment(sketch, "E113", {"start": v(-1661.22, -2379.78) * mm, "end": v(1661.22, -2379.78) * mm, "construction": true});
            skPoint(sketch, "E114", {"position": v(1661.22, -2379.78) * mm});
            skLineSegment(sketch, "E115.0.MirrorCS", {"start": v(-85.4, -2898.7) * mm, "end": v(-1592.64, -2898.7) * mm});
            skLineSegment(sketch, "E116.0.MirrorCS", {"start": v(-1592.64, -2917.5) * mm, "end": v(-839.03, -2917.5) * mm});
            skLineSegment(sketch, "E117.0.MirrorCS", {"start": v(-1592.64, -2898.7) * mm, "end": v(-1592.64, -2917.5) * mm});
            skCircle(sketch, "E118.0.MirrorC", {"center": v(-1561.66, -2908.1) * mm, "radius": 3.56 * mm});
            skCircle(sketch, "E119.0.MirrorC", {"center": v(-1381.06, -2908.1) * mm, "radius": 4.76 * mm});
            skLineSegment(sketch, "E120.0.MirrorCS", {"start": v(-839.03, -2917.5) * mm, "end": v(-85.4, -2917.5) * mm});
            skLineSegment(sketch, "E121.0.MirrorCS", {"start": v(-85.4, -2917.5) * mm, "end": v(-85.4, -2898.7) * mm});
            skCircle(sketch, "E122.0.MirrorC", {"center": v(-296.99, -2908.1) * mm, "radius": 4.76 * mm});
            skCircle(sketch, "E123.0.MirrorC", {"center": v(-296.99, -3859.84) * mm, "radius": 4.76 * mm});
            skLineSegment(sketch, "E124.0.MirrorCS", {"start": v(-839.03, -3850.44) * mm, "end": v(-85.4, -3850.44) * mm});
            skLineSegment(sketch, "E125.0.MirrorCS", {"start": v(-85.4, -3850.44) * mm, "end": v(-85.4, -3869.23) * mm});
            skLineSegment(sketch, "E126.0.MirrorCS", {"start": v(-85.4, -3869.23) * mm, "end": v(-1592.64, -3869.23) * mm});
            skLineSegment(sketch, "E127.0.MirrorCS", {"start": v(-1592.64, -3850.44) * mm, "end": v(-839.03, -3850.44) * mm});
            skCircle(sketch, "E128.0.MirrorC", {"center": v(-1381.06, -3859.84) * mm, "radius": 4.76 * mm});
            skCircle(sketch, "E129.0.MirrorC", {"center": v(-1561.66, -3859.84) * mm, "radius": 3.56 * mm});
            skLineSegment(sketch, "E130.0.MirrorCS", {"start": v(-1592.64, -3869.23) * mm, "end": v(-1592.64, -3850.44) * mm});
            skCircle(sketch, "E131.0.MirrorC", {"center": v(-296.99, -2855.65) * mm, "radius": 4.76 * mm});
            skLineSegment(sketch, "E132.0.MirrorCS", {"start": v(85.4, -909.12) * mm, "end": v(85.4, -890.32) * mm});
            skLineSegment(sketch, "E133.0.MirrorCS", {"start": v(839.03, -909.12) * mm, "end": v(85.4, -909.12) * mm});
            skLineSegment(sketch, "E134.0.MirrorCS", {"start": v(85.4, -890.32) * mm, "end": v(1592.64, -890.32) * mm});
            skCircle(sketch, "E135.0.MirrorC", {"center": v(296.99, -899.72) * mm, "radius": 4.76 * mm});
            skLineSegment(sketch, "E136.1.MirrorCS", {"start": v(1592.64, -890.32) * mm, "end": v(1592.64, -909.12) * mm});
            skCircle(sketch, "E136.3.MirrorC", {"center": v(1561.66, -899.72) * mm, "radius": 3.56 * mm});
            skCircle(sketch, "E136.4.MirrorC", {"center": v(1381.06, -899.72) * mm, "radius": 4.76 * mm});
            skLineSegment(sketch, "E136.6.MirrorCS", {"start": v(1592.64, -899.72) * mm, "end": v(85.4, -899.72) * mm, "construction": true});
            skLineSegment(sketch, "E136.8.MirrorCS", {"start": v(1592.64, -909.12) * mm, "end": v(839.03, -909.12) * mm});
            skLineSegment(sketch, "E137.0.MirrorCS", {"start": v(85.4, -1913.3) * mm, "end": v(85.4, -1894.51) * mm});
            skLineSegment(sketch, "E137.1.MirrorCS", {"start": v(1592.64, -1894.51) * mm, "end": v(1592.64, -1913.3) * mm});
            skCircle(sketch, "E137.2.MirrorC", {"center": v(296.99, -1851.46) * mm, "radius": 4.76 * mm});
            skCircle(sketch, "E137.3.MirrorC", {"center": v(1561.66, -1851.46) * mm, "radius": 3.56 * mm});
            skLineSegment(sketch, "E137.4.MirrorCS", {"start": v(85.4, -1842.06) * mm, "end": v(85.4, -1860.86) * mm});
            skLineSegment(sketch, "E137.5.MirrorCS", {"start": v(1592.64, -1860.86) * mm, "end": v(1592.64, -1842.06) * mm});
            skCircle(sketch, "E137.6.MirrorC", {"center": v(1561.66, -1903.9) * mm, "radius": 3.56 * mm});
            skCircle(sketch, "E137.7.MirrorC", {"center": v(296.99, -1903.9) * mm, "radius": 4.76 * mm});
            skCircle(sketch, "E137.8.MirrorC", {"center": v(1381.06, -1903.9) * mm, "radius": 4.76 * mm});
            skLineSegment(sketch, "E137.9.MirrorCS", {"start": v(839.03, -1842.06) * mm, "end": v(85.4, -1842.06) * mm});
            skLineSegment(sketch, "E137.10.MirrorCS", {"start": v(1592.64, -1842.06) * mm, "end": v(839.03, -1842.06) * mm});
            skCircle(sketch, "E137.11.MirrorC", {"center": v(1381.06, -1851.46) * mm, "radius": 4.76 * mm});
            skLineSegment(sketch, "E137.12.MirrorCS", {"start": v(85.4, -1860.86) * mm, "end": v(1592.64, -1860.86) * mm});
            skLineSegment(sketch, "E137.13.MirrorCS", {"start": v(85.4, -1894.51) * mm, "end": v(1592.64, -1894.51) * mm});
            skLineSegment(sketch, "E137.14.MirrorCS", {"start": v(839.03, -1913.3) * mm, "end": v(85.4, -1913.3) * mm});
            skLineSegment(sketch, "E137.15.MirrorCS", {"start": v(1592.64, -1913.3) * mm, "end": v(839.03, -1913.3) * mm});
            skLineSegment(sketch, "E138.0.MirrorCS", {"start": v(1592.64, -2898.7) * mm, "end": v(1592.64, -2917.5) * mm});
            skCircle(sketch, "E138.1.MirrorC", {"center": v(296.99, -2855.65) * mm, "radius": 4.76 * mm});
            skCircle(sketch, "E138.2.MirrorC", {"center": v(1381.06, -2855.65) * mm, "radius": 4.76 * mm});
            skCircle(sketch, "E138.3.MirrorC", {"center": v(1561.66, -2855.65) * mm, "radius": 3.56 * mm});
            skLineSegment(sketch, "E138.4.MirrorCS", {"start": v(1592.64, -2865.05) * mm, "end": v(1592.64, -2846.25) * mm});
            skCircle(sketch, "E138.5.MirrorC", {"center": v(1381.06, -2908.1) * mm, "radius": 4.76 * mm});
            skCircle(sketch, "E138.6.MirrorC", {"center": v(1561.66, -2908.1) * mm, "radius": 3.56 * mm});
            skCircle(sketch, "E138.7.MirrorC", {"center": v(296.99, -2908.1) * mm, "radius": 4.76 * mm});
            skLineSegment(sketch, "E138.8.MirrorCS", {"start": v(839.03, -2846.25) * mm, "end": v(85.4, -2846.25) * mm});
            skLineSegment(sketch, "E138.9.MirrorCS", {"start": v(1592.64, -2846.25) * mm, "end": v(839.03, -2846.25) * mm});
            skLineSegment(sketch, "E138.10.MirrorCS", {"start": v(85.4, -2846.25) * mm, "end": v(85.4, -2865.05) * mm});
            skLineSegment(sketch, "E138.11.MirrorCS", {"start": v(85.4, -2865.05) * mm, "end": v(1592.64, -2865.05) * mm});
            skLineSegment(sketch, "E138.12.MirrorCS", {"start": v(85.4, -2865.05) * mm, "end": v(1592.64, -2865.05) * mm});
            skLineSegment(sketch, "E138.13.MirrorCS", {"start": v(85.4, -2898.7) * mm, "end": v(1592.64, -2898.7) * mm});
            skLineSegment(sketch, "E138.14.MirrorCS", {"start": v(85.4, -2898.7) * mm, "end": v(1592.64, -2898.7) * mm});
            skLineSegment(sketch, "E138.15.MirrorCS", {"start": v(85.4, -2917.5) * mm, "end": v(85.4, -2898.7) * mm});
            skLineSegment(sketch, "E138.16.MirrorCS", {"start": v(839.03, -2917.5) * mm, "end": v(85.4, -2917.5) * mm});
            skLineSegment(sketch, "E138.17.MirrorCS", {"start": v(1592.64, -2917.5) * mm, "end": v(839.03, -2917.5) * mm});
            skCircle(sketch, "E139.0.MirrorC", {"center": v(1561.66, -3859.84) * mm, "radius": 3.56 * mm});
            skLineSegment(sketch, "E139.1.MirrorCS", {"start": v(85.4, -3850.44) * mm, "end": v(85.4, -3869.23) * mm});
            skCircle(sketch, "E139.2.MirrorC", {"center": v(296.99, -3859.84) * mm, "radius": 4.76 * mm});
            skLineSegment(sketch, "E139.3.MirrorCS", {"start": v(1592.64, -3869.23) * mm, "end": v(1592.64, -3850.44) * mm});
            skLineSegment(sketch, "E139.4.MirrorCS", {"start": v(839.03, -3850.44) * mm, "end": v(85.4, -3850.44) * mm});
            skLineSegment(sketch, "E139.5.MirrorCS", {"start": v(1592.64, -3850.44) * mm, "end": v(839.03, -3850.44) * mm});
            skCircle(sketch, "E139.6.MirrorC", {"center": v(1381.06, -3859.84) * mm, "radius": 4.76 * mm});
            skLineSegment(sketch, "E139.7.MirrorCS", {"start": v(85.4, -3869.23) * mm, "end": v(1592.64, -3869.23) * mm});
            skSolve(sketch);
        }
        {
            var Q0;
            Q0=makeQuery(id+"F23.imprint","IMPRINT",FACE,{"disambiguationData":[TD([[makeQuery(id+"F23.imprint","IMPRINT",EDGE,{"derivedFrom":sQuery(id+"F23.wireOp",EDGE,"E80")}),1.0]])]});
            var Q1;
            Q1=makeQuery(id+"F23.imprint","IMPRINT",FACE,{"disambiguationData":[TD([[makeQuery(id+"F23.imprint","IMPRINT",EDGE,{"derivedFrom":sQuery(id+"F23.wireOp",EDGE,"E132.0.MirrorCS")}),-1.0]])]});
            var Q2;
            Q2=makeQuery(id+"F23.imprint","IMPRINT",FACE,{"disambiguationData":[TD([[makeQuery(id+"F23.imprint","IMPRINT",EDGE,{"derivedFrom":sQuery(id+"F23.wireOp",EDGE,"E97.0.MirrorC")}),1.0]])]});
            var Q3;
            Q3=makeQuery(id+"F23.imprint","IMPRINT",FACE,{"disambiguationData":[TD([[makeQuery(id+"F23.imprint","IMPRINT",EDGE,{"derivedFrom":sQuery(id+"F23.wireOp",EDGE,"E98.0.MirrorCS")}),1.0]])]});
            var Q4;
            Q4=makeQuery(id+"F23.imprint","IMPRINT",FACE,{"disambiguationData":[TD([[makeQuery(id+"F23.imprint","IMPRINT",EDGE,{"derivedFrom":sQuery(id+"F23.wireOp",EDGE,"E137.2.MirrorC")}),1.0]])]});
            var Q5;
            Q5=makeQuery(id+"F23.imprint","IMPRINT",FACE,{"disambiguationData":[TD([[makeQuery(id+"F23.imprint","IMPRINT",EDGE,{"derivedFrom":sQuery(id+"F23.wireOp",EDGE,"E137.0.MirrorCS")}),-1.0]])]});
            var Q6;
            Q6=makeQuery(id+"F23.imprint","IMPRINT",FACE,{"disambiguationData":[TD([[makeQuery(id+"F23.imprint","IMPRINT",EDGE,{"derivedFrom":sQuery(id+"F23.wireOp",EDGE,"E138.0.MirrorCS")}),-1.0]])]});
            var Q7;
            Q7=makeQuery(id+"F23.imprint","IMPRINT",FACE,{"disambiguationData":[TD([[makeQuery(id+"F23.imprint","IMPRINT",EDGE,{"derivedFrom":sQuery(id+"F23.wireOp",EDGE,"E138.1.MirrorC")}),1.0]])]});
            var Q8;
            Q8=makeQuery(id+"F23.imprint","IMPRINT",FACE,{"disambiguationData":[TD([[makeQuery(id+"F23.imprint","IMPRINT",EDGE,{"derivedFrom":sQuery(id+"F23.wireOp",EDGE,"E106.0.MirrorCS")}),-1.0]])]});
            var Q9;
            Q9=makeQuery(id+"F23.imprint","IMPRINT",FACE,{"disambiguationData":[TD([[makeQuery(id+"F23.imprint","IMPRINT",EDGE,{"derivedFrom":sQuery(id+"F23.wireOp",EDGE,"E116.0.MirrorCS")}),1.0]])]});
            var Q10;
            Q10=makeQuery(id+"F23.imprint","IMPRINT",FACE,{"disambiguationData":[TD([[makeQuery(id+"F23.imprint","IMPRINT",EDGE,{"derivedFrom":sQuery(id+"F23.wireOp",EDGE,"E123.0.MirrorC")}),-1.0]])]});
            var Q11;
            Q11=makeQuery(id+"F23.imprint","IMPRINT",FACE,{"disambiguationData":[TD([[makeQuery(id+"F23.imprint","IMPRINT",EDGE,{"derivedFrom":sQuery(id+"F23.wireOp",EDGE,"E139.0.MirrorC")}),-1.0]])]});
            extrude(context, id + "F24", {"entities" : qUnion([Q0, Q1, Q2, Q3, Q4, Q5, Q6, Q7, Q8, Q9, Q10, Q11]), "operationType" : NewBodyOperationType.ADD, "oppositeDirection" : true, "depth" : 2.54 * mm});
        }
        {
            var Q0;
            Q0=qCreatedBy(id+"F20.planeOp",FACE);
            var sketch = newSketch(context, id + "F25", { "sketchPlane" : qUnion([Q0])});
            skLineSegment(sketch, "E140", {"start": v(-1362.42, 2623.08) * mm, "end": v(-1406.87, 2623.08) * mm});
            skLineSegment(sketch, "E141", {"start": v(-1406.87, 2623.08) * mm, "end": v(-1406.87, 2521.48) * mm});
            skLineSegment(sketch, "E142", {"start": v(-1406.87, 2521.48) * mm, "end": v(-1362.42, 2521.48) * mm});
            skLineSegment(sketch, "E143", {"start": v(-1362.42, 2521.48) * mm, "end": v(-1362.42, 2527.83) * mm});
            skLineSegment(sketch, "E144", {"start": v(-1362.42, 2623.08) * mm, "end": v(-1362.42, 2616.73) * mm});
            skLineSegment(sketch, "E145", {"start": v(-1362.42, 2616.73) * mm, "end": v(-1400.52, 2616.73) * mm});
            skLineSegment(sketch, "E146", {"start": v(-1400.52, 2616.73) * mm, "end": v(-1400.52, 2527.83) * mm});
            skLineSegment(sketch, "E147", {"start": v(-1400.52, 2527.83) * mm, "end": v(-1362.42, 2527.83) * mm});
            skLineSegment(sketch, "E148.0.MirrorCS", {"start": v(1362.42, 2623.08) * mm, "end": v(1406.87, 2623.08) * mm});
            skLineSegment(sketch, "E148.1.MirrorCS", {"start": v(1400.52, 2527.83) * mm, "end": v(1362.42, 2527.83) * mm});
            skLineSegment(sketch, "E148.2.MirrorCS", {"start": v(1362.42, 2521.48) * mm, "end": v(1362.42, 2527.83) * mm});
            skLineSegment(sketch, "E148.3.MirrorCS", {"start": v(1406.87, 2521.48) * mm, "end": v(1362.42, 2521.48) * mm});
            skLineSegment(sketch, "E148.4.MirrorCS", {"start": v(1362.42, 2616.73) * mm, "end": v(1400.52, 2616.73) * mm});
            skLineSegment(sketch, "E148.5.MirrorCS", {"start": v(1406.87, 2623.08) * mm, "end": v(1406.87, 2521.48) * mm});
            skLineSegment(sketch, "E148.6.MirrorCS", {"start": v(1400.52, 2616.73) * mm, "end": v(1400.52, 2527.83) * mm});
            skLineSegment(sketch, "E148.7.MirrorCS", {"start": v(1362.42, 2623.08) * mm, "end": v(1362.42, 2616.73) * mm});
            skLineSegment(sketch, "E149", {"start": v(0, 2144.38) * mm, "end": v(839.24, 2144.38) * mm, "construction": true});
            skLineSegment(sketch, "E150", {"start": v(839.24, 2144.38) * mm, "end": v(839.24, 3023.37) * mm, "construction": true});
            skLineSegment(sketch, "E151", {"start": v(839.24, 3023.37) * mm, "end": v(-839.24, 3023.37) * mm, "construction": true});
            skLineSegment(sketch, "E152", {"start": v(-839.24, 3023.37) * mm, "end": v(-839.24, 2144.38) * mm, "construction": true});
            skLineSegment(sketch, "E153", {"start": v(-839.24, 2144.38) * mm, "end": v(0, 2144.38) * mm, "construction": true});
            skLineSegment(sketch, "E154.0.MirrorCS", {"start": v(316.05, 2623.08) * mm, "end": v(316.05, 2616.73) * mm});
            skLineSegment(sketch, "E154.1.MirrorCS", {"start": v(316.05, 2616.73) * mm, "end": v(277.95, 2616.73) * mm});
            skLineSegment(sketch, "E154.2.MirrorCS", {"start": v(277.95, 2527.83) * mm, "end": v(316.05, 2527.83) * mm});
            skLineSegment(sketch, "E154.3.MirrorCS", {"start": v(316.05, 2521.48) * mm, "end": v(316.05, 2527.83) * mm});
            skLineSegment(sketch, "E154.4.MirrorCS", {"start": v(316.05, 2623.08) * mm, "end": v(271.6, 2623.08) * mm});
            skLineSegment(sketch, "E154.5.MirrorCS", {"start": v(277.95, 2616.73) * mm, "end": v(277.95, 2527.83) * mm});
            skLineSegment(sketch, "E154.6.MirrorCS", {"start": v(271.6, 2521.48) * mm, "end": v(316.05, 2521.48) * mm});
            skLineSegment(sketch, "E154.7.MirrorCS", {"start": v(271.6, 2623.08) * mm, "end": v(271.6, 2521.48) * mm});
            skLineSegment(sketch, "E155.0.MirrorCS", {"start": v(-316.05, 2521.48) * mm, "end": v(-316.05, 2527.83) * mm});
            skLineSegment(sketch, "E155.1.MirrorCS", {"start": v(-316.05, 2623.08) * mm, "end": v(-271.6, 2623.08) * mm});
            skLineSegment(sketch, "E155.2.MirrorCS", {"start": v(-316.05, 2623.08) * mm, "end": v(-316.05, 2616.73) * mm});
            skLineSegment(sketch, "E155.3.MirrorCS", {"start": v(-316.05, 2616.73) * mm, "end": v(-277.95, 2616.73) * mm});
            skLineSegment(sketch, "E155.4.MirrorCS", {"start": v(-271.6, 2623.08) * mm, "end": v(-271.6, 2521.48) * mm});
            skLineSegment(sketch, "E155.5.MirrorCS", {"start": v(-277.95, 2616.73) * mm, "end": v(-277.95, 2527.83) * mm});
            skLineSegment(sketch, "E155.6.MirrorCS", {"start": v(-271.6, 2521.48) * mm, "end": v(-316.05, 2521.48) * mm});
            skLineSegment(sketch, "E155.7.MirrorCS", {"start": v(-277.95, 2527.83) * mm, "end": v(-316.05, 2527.83) * mm});
            skLineSegment(sketch, "E156", {"start": v(1381.47, 2527.83) * mm, "end": v(1381.47, 2629.03) * mm, "construction": true});
            skLineSegment(sketch, "E157", {"start": v(297, 2527.83) * mm, "end": v(297, 2660.85) * mm, "construction": true});
            skSolve(sketch);
        }
        {
            var Q0;
            Q0=makeQuery(id+"F25.imprint","IMPRINT",FACE,{"disambiguationData":[TD([[makeQuery(id+"F25.imprint","IMPRINT",EDGE,{"derivedFrom":sQuery(id+"F25.wireOp",EDGE,"E140")}),1.0]])]});
            var Q1;
            Q1=makeQuery(id+"F25.imprint","IMPRINT",FACE,{"disambiguationData":[TD([[makeQuery(id+"F25.imprint","IMPRINT",EDGE,{"derivedFrom":sQuery(id+"F25.wireOp",EDGE,"E155.0.MirrorCS")}),-1.0]])]});
            var Q2;
            Q2=makeQuery(id+"F25.imprint","IMPRINT",FACE,{"disambiguationData":[TD([[makeQuery(id+"F25.imprint","IMPRINT",EDGE,{"derivedFrom":sQuery(id+"F25.wireOp",EDGE,"E154.0.MirrorCS")}),-1.0]])]});
            var Q3;
            Q3=makeQuery(id+"F25.imprint","IMPRINT",FACE,{"disambiguationData":[TD([[makeQuery(id+"F25.imprint","IMPRINT",EDGE,{"derivedFrom":sQuery(id+"F25.wireOp",EDGE,"E148.0.MirrorCS")}),-1.0]])]});
            extrude(context, id + "F26", {"entities" : qUnion([Q0, Q1, Q2, Q3]), "depth" : 1524 * mm, "hasSecondDirection" : true, "secondDirectionOppositeDirection" : true, "secondDirectionDepth" : 1524 * mm});
        }
        {
            var Q0;
            Q0=qCreatedBy(makeId("Right.planeOp"),FACE);
            var sketch = newSketch(context, id + "F27", { "sketchPlane" : qUnion([Q0])});
            skCircle(sketch, "E158", {"center": v(0, 3425.83) * mm, "radius": 57.15 * mm});
            skLineSegment(sketch, "E159", {"start": v(0, 3482.97) * mm, "end": v(1524, 3482.97) * mm});
            skLineSegment(sketch, "E160", {"start": v(0, 3482.97) * mm, "end": v(-1524, 3482.98) * mm});
            skLineSegment(sketch, "E161", {"start": v(-1524, 3482.97) * mm, "end": v(-1524, 3584.57) * mm});
            skLineSegment(sketch, "E162", {"start": v(-1524, 3584.57) * mm, "end": v(1524, 3584.57) * mm});
            skLineSegment(sketch, "E163", {"start": v(1524, 3584.58) * mm, "end": v(1524, 3482.97) * mm});
            skLineSegment(sketch, "E164", {"start": v(0, 3482.97) * mm, "end": v(0, 3425.83) * mm, "construction": true});
            skLineSegment(sketch, "E165", {"start": v(-157.1, 3425.83) * mm, "end": v(0, 3425.83) * mm});
            skLineSegment(sketch, "E166", {"start": v(0, 3425.83) * mm, "end": v(88.8, 3425.83) * mm});
            skPoint(sketch, "E167", {"position": v(88.8, 3425.83) * mm});
            skLineSegment(sketch, "E168.1.0", {"start": v(-53.73, 3278.2) * mm, "end": v(0, 3425.83) * mm});
            skLineSegment(sketch, "E168.1.1", {"start": v(-53.7, 3445.37) * mm, "end": v(467.54, 4877.46) * mm});
            skLineSegment(sketch, "E168.1.2", {"start": v(-670.41, 2048.03) * mm, "end": v(372.06, 4912.21) * mm});
            skLineSegment(sketch, "E168.1.3", {"start": v(-53.7, 3445.37) * mm, "end": v(-574.94, 2013.28) * mm});
            skLineSegment(sketch, "E168.anchor1", {"start": v(0, 3425.83) * mm, "end": v(-157.1, 3425.83) * mm, "construction": true});
            skLineSegment(sketch, "E168.anchor2", {"start": v(0, 3425.83) * mm, "end": v(-53.73, 3278.2) * mm, "construction": true});
            skCircle(sketch, "E169", {"center": v(0, 3425.83) * mm, "radius": 457.2 * mm, "construction": true});
            skLineSegment(sketch, "E170", {"start": v(0, 3425.83) * mm, "end": v(453.61, 3482.97) * mm});
            skLineSegment(sketch, "E171", {"start": v(101.44, 3871.63) * mm, "end": v(0, 3425.83) * mm});
            skLineSegment(sketch, "E172", {"start": v(372.06, 4912.21) * mm, "end": v(467.54, 4877.46) * mm});
            skLineSegment(sketch, "E173", {"start": v(-670.41, 2048.03) * mm, "end": v(-574.94, 2013.28) * mm});
            skLineSegment(sketch, "E174.0", {"start": v(-84.14, 1993.9) * mm, "end": v(84.14, 1993.9) * mm});
            skLineSegment(sketch, "E175", {"start": v(-84.14, 1993.9) * mm, "end": v(-84.14, 2334.47) * mm, "construction": true});
            skLineSegment(sketch, "E176", {"start": v(84.14, 1993.9) * mm, "end": v(84.14, 2318.03) * mm, "construction": true});
            skLineSegment(sketch, "E177", {"start": v(0, 3425.83) * mm, "end": v(-453.61, 3482.97) * mm});
            skLineSegment(sketch, "E178", {"start": v(-208.85, 3019.11) * mm, "end": v(0, 3425.83) * mm});
            skLineSegment(sketch, "E179", {"start": v(-453.61, 3482.97) * mm, "end": v(0, 3106.99) * mm});
            skLineSegment(sketch, "E180", {"start": v(-208.85, 3019.11) * mm, "end": v(0, 3106.99) * mm});
            skLineSegment(sketch, "E181", {"start": v(0, 3106.99) * mm, "end": v(702.36, 3402.51) * mm});
            skLineSegment(sketch, "E182", {"start": v(0, 3106.99) * mm, "end": v(586.67, 2620.71) * mm});
            skSolve(sketch);
        }
        {
            var Q0;
            Q0=qCreatedBy(makeId("Front.planeOp"),FACE);
            var sketch = newSketch(context, id + "F28", { "sketchPlane" : qUnion([Q0])});
            skLineSegment(sketch, "E183.rect.bottom", {"start": v(127, 3081.59) * mm, "end": v(76.2, 3081.59) * mm});
            skLineSegment(sketch, "E183.rect.top", {"start": v(127, 3132.39) * mm, "end": v(76.2, 3132.39) * mm});
            skLineSegment(sketch, "E183.rect.left", {"start": v(127, 3081.59) * mm, "end": v(127, 3132.39) * mm});
            skLineSegment(sketch, "E183.rect.right", {"start": v(76.2, 3081.59) * mm, "end": v(76.2, 3132.39) * mm});
            skPoint(sketch, "E183.rect.middle", {"position": v(101.6, 3106.99) * mm});
            skLineSegment(sketch, "E184", {"start": v(0, 3106.99) * mm, "end": v(101.6, 3106.99) * mm});
            skLineSegment(sketch, "E185.0", {"start": v(76.2, 2908.3) * mm, "end": v(76.2, 3365.5) * mm, "construction": true});
            skLineSegment(sketch, "E186.0", {"start": v(122.24, 3086.35) * mm, "end": v(122.24, 3127.63) * mm});
            skLineSegment(sketch, "E186.1", {"start": v(122.24, 3086.35) * mm, "end": v(80.96, 3086.35) * mm});
            skLineSegment(sketch, "E186.2", {"start": v(80.96, 3086.35) * mm, "end": v(80.96, 3127.63) * mm});
            skLineSegment(sketch, "E186.3", {"start": v(122.24, 3127.63) * mm, "end": v(80.96, 3127.63) * mm});
            skSolve(sketch);
        }
        {
            var Q0;
            {var subQ6=sQuery(id+"F28.wireOp",EDGE,"E183.rect.bottom");Q0=makeQuery(id+"F28.imprint","IMPRINT",FACE,{"disambiguationData":[TD([[makeQuery(id+"F28.imprint","IMPRINT",EDGE,{"derivedFrom":subQ6}),-1.0]])]});}
            extrude(context, id + "F29", {"entities" : qUnion([Q0]), "operationType" : NewBodyOperationType.ADD, "depth" : 50.8 * mm, "hasSecondDirection" : true, "secondDirectionOppositeDirection" : true, "secondDirectionDepth" : 50.8 * mm});
        }
        {
            var Q0;
            Q0=makeQuery(id+"F17.opExtrude","SWEPT_FACE",FACE,{"disambiguationData":[OSD([sQuery(id+"F15.wireOp",EDGE,"E44")])]});
            var sketch = newSketch(context, id + "F30", { "sketchPlane" : qUnion([Q0])});
            skLineSegment(sketch, "E187.bottom", {"start": v(258.9, 2459.4) * mm, "end": v(335.07, 2459.4) * mm});
            skLineSegment(sketch, "E187.top", {"start": v(258.9, 2300.15) * mm, "end": v(335.07, 2300.15) * mm});
            skLineSegment(sketch, "E187.left", {"start": v(233.5, 2434) * mm, "end": v(233.5, 2325.55) * mm});
            skLineSegment(sketch, "E187.right", {"start": v(360.47, 2434) * mm, "end": v(360.47, 2325.55) * mm});
            skLineSegment(sketch, "E188", {"start": v(296.99, 3859.84) * mm, "end": v(296.99, 2300.15) * mm, "construction": true});
            skLineSegment(sketch, "E189", {"start": v(233.5, 2379.78) * mm, "end": v(360.47, 2379.78) * mm, "construction": true});
            skLineSegment(sketch, "E190", {"start": v(1381.06, 3859.84) * mm, "end": v(1381.06, 2310.56) * mm, "construction": true});
            skCircle(sketch, "E191", {"center": v(252.55, 2379.78) * mm, "radius": 4.76 * mm});
            skCircle(sketch, "E192", {"center": v(252.55, 2379.78) * mm, "radius": 19.05 * mm, "construction": true});
            skCircle(sketch, "E193.0.MirrorC", {"center": v(341.42, 2379.78) * mm, "radius": 4.76 * mm});
            skPoint(sketch, "E194.visualSharp", {"position": v(233.5, 2459.4) * mm});
            skArc(sketch, "E194.filletArc", {"start": v(258.9, 2459.4) * mm, "mid": v(240.94, 2451.97) * mm, "end": v(233.5, 2434) * mm});
            skPoint(sketch, "E195.visualSharp", {"position": v(360.47, 2459.4) * mm});
            skArc(sketch, "E195.filletArc", {"start": v(360.47, 2434) * mm, "mid": v(353.04, 2451.97) * mm, "end": v(335.07, 2459.4) * mm});
            skPoint(sketch, "E196.visualSharp", {"position": v(360.47, 2300.15) * mm});
            skArc(sketch, "E196.filletArc", {"start": v(335.07, 2300.15) * mm, "mid": v(353.04, 2307.59) * mm, "end": v(360.47, 2325.55) * mm});
            skPoint(sketch, "E197.visualSharp", {"position": v(233.5, 2300.15) * mm});
            skArc(sketch, "E197.filletArc", {"start": v(233.5, 2325.55) * mm, "mid": v(240.94, 2307.59) * mm, "end": v(258.9, 2300.15) * mm});
            skCircle(sketch, "E198", {"center": v(296.99, 2438.08) * mm, "radius": 6.35 * mm});
            skCircle(sketch, "E199.0.MirrorC", {"center": v(296.99, 2321.47) * mm, "radius": 6.35 * mm});
            skCircle(sketch, "E200", {"center": v(296.99, 2438.08) * mm, "radius": 9 * mm, "construction": true});
            skLineSegment(sketch, "E201", {"start": v(296.99, 2379.78) * mm, "end": v(1381.06, 2379.78) * mm, "construction": true});
            skLineSegment(sketch, "E202", {"start": v(839.03, 2730.65) * mm, "end": v(839.03, 2379.78) * mm, "construction": true});
            skLineSegment(sketch, "E203.0.MirrorCS", {"start": v(1444.55, 2434) * mm, "end": v(1444.55, 2325.55) * mm});
            skArc(sketch, "E203.1.MirrorCS", {"start": v(1444.55, 2325.55) * mm, "mid": v(1437.1, 2307.59) * mm, "end": v(1419.15, 2300.15) * mm});
            skLineSegment(sketch, "E203.2.MirrorCS", {"start": v(1419.15, 2300.15) * mm, "end": v(1342.98, 2300.15) * mm});
            skArc(sketch, "E203.3.MirrorCS", {"start": v(1342.98, 2300.15) * mm, "mid": v(1325.02, 2307.59) * mm, "end": v(1317.58, 2325.55) * mm});
            skLineSegment(sketch, "E203.4.MirrorCS", {"start": v(1317.58, 2434) * mm, "end": v(1317.58, 2325.55) * mm});
            skArc(sketch, "E203.5.MirrorCS", {"start": v(1317.58, 2434) * mm, "mid": v(1325.02, 2451.97) * mm, "end": v(1342.98, 2459.4) * mm});
            skLineSegment(sketch, "E203.6.MirrorCS", {"start": v(1419.15, 2459.4) * mm, "end": v(1342.98, 2459.4) * mm});
            skArc(sketch, "E203.7.MirrorCS", {"start": v(1419.15, 2459.4) * mm, "mid": v(1437.1, 2451.97) * mm, "end": v(1444.55, 2434) * mm});
            skCircle(sketch, "E203.8.MirrorC", {"center": v(1425.5, 2379.78) * mm, "radius": 4.76 * mm});
            skCircle(sketch, "E203.9.MirrorC", {"center": v(1336.63, 2379.78) * mm, "radius": 4.76 * mm});
            skCircle(sketch, "E203.10.MirrorC", {"center": v(1381.06, 2321.47) * mm, "radius": 6.35 * mm});
            skCircle(sketch, "E203.11.MirrorC", {"center": v(1381.06, 2438.08) * mm, "radius": 6.35 * mm});
            skCircle(sketch, "E204.0.MirrorC", {"center": v(-1381.06, 2438.08) * mm, "radius": 6.35 * mm});
            skCircle(sketch, "E204.1.MirrorC", {"center": v(-296.99, 2438.08) * mm, "radius": 6.35 * mm});
            skCircle(sketch, "E204.2.MirrorC", {"center": v(-296.99, 2438.08) * mm, "radius": 9 * mm, "construction": true});
            skArc(sketch, "E204.3.MirrorCS", {"start": v(-360.47, 2434) * mm, "mid": v(-353.04, 2451.97) * mm, "end": v(-335.07, 2459.4) * mm});
            skCircle(sketch, "E204.4.MirrorC", {"center": v(-1425.5, 2379.78) * mm, "radius": 4.76 * mm});
            skCircle(sketch, "E204.5.MirrorC", {"center": v(-1336.63, 2379.78) * mm, "radius": 4.76 * mm});
            skCircle(sketch, "E204.6.MirrorC", {"center": v(-341.42, 2379.78) * mm, "radius": 4.76 * mm});
            skCircle(sketch, "E204.7.MirrorC", {"center": v(-252.55, 2379.78) * mm, "radius": 4.76 * mm});
            skCircle(sketch, "E204.8.MirrorC", {"center": v(-1381.06, 2321.47) * mm, "radius": 6.35 * mm});
            skArc(sketch, "E204.9.MirrorCS", {"start": v(-335.07, 2300.15) * mm, "mid": v(-353.04, 2307.59) * mm, "end": v(-360.47, 2325.55) * mm});
            skCircle(sketch, "E204.10.MirrorC", {"center": v(-296.99, 2321.47) * mm, "radius": 6.35 * mm});
            skLineSegment(sketch, "E204.11.MirrorCS", {"start": v(-258.9, 2459.4) * mm, "end": v(-335.07, 2459.4) * mm});
            skLineSegment(sketch, "E204.12.MirrorCS", {"start": v(-1419.15, 2459.4) * mm, "end": v(-1342.98, 2459.4) * mm});
            skArc(sketch, "E204.13.MirrorCS", {"start": v(-1317.58, 2434) * mm, "mid": v(-1325.02, 2451.97) * mm, "end": v(-1342.98, 2459.4) * mm});
            skArc(sketch, "E204.14.MirrorCS", {"start": v(-1419.15, 2459.4) * mm, "mid": v(-1437.1, 2451.97) * mm, "end": v(-1444.55, 2434) * mm});
            skArc(sketch, "E204.15.MirrorCS", {"start": v(-258.9, 2459.4) * mm, "mid": v(-240.94, 2451.97) * mm, "end": v(-233.5, 2434) * mm});
            skPoint(sketch, "E204.16.MirrorP", {"position": v(-360.47, 2459.4) * mm});
            skPoint(sketch, "E204.17.MirrorP", {"position": v(-233.5, 2459.4) * mm});
            skLineSegment(sketch, "E204.18.MirrorCS", {"start": v(-839.03, 2730.65) * mm, "end": v(-839.03, 2379.78) * mm, "construction": true});
            skLineSegment(sketch, "E204.19.MirrorCS", {"start": v(-233.5, 2379.78) * mm, "end": v(-360.47, 2379.78) * mm, "construction": true});
            skLineSegment(sketch, "E204.20.MirrorCS", {"start": v(-296.99, 2379.78) * mm, "end": v(-1381.06, 2379.78) * mm, "construction": true});
            skCircle(sketch, "E204.21.MirrorC", {"center": v(-252.55, 2379.78) * mm, "radius": 19.05 * mm, "construction": true});
            skLineSegment(sketch, "E204.22.MirrorCS", {"start": v(-1444.55, 2434) * mm, "end": v(-1444.55, 2325.55) * mm});
            skLineSegment(sketch, "E204.23.MirrorCS", {"start": v(-1317.58, 2434) * mm, "end": v(-1317.58, 2325.55) * mm});
            skLineSegment(sketch, "E204.24.MirrorCS", {"start": v(-360.47, 2434) * mm, "end": v(-360.47, 2325.55) * mm});
            skLineSegment(sketch, "E204.25.MirrorCS", {"start": v(-233.5, 2434) * mm, "end": v(-233.5, 2325.55) * mm});
            skArc(sketch, "E204.26.MirrorCS", {"start": v(-1444.55, 2325.55) * mm, "mid": v(-1437.1, 2307.59) * mm, "end": v(-1419.15, 2300.15) * mm});
            skArc(sketch, "E204.27.MirrorCS", {"start": v(-1342.98, 2300.15) * mm, "mid": v(-1325.02, 2307.59) * mm, "end": v(-1317.58, 2325.55) * mm});
            skArc(sketch, "E204.28.MirrorCS", {"start": v(-233.5, 2325.55) * mm, "mid": v(-240.94, 2307.59) * mm, "end": v(-258.9, 2300.15) * mm});
            skLineSegment(sketch, "E204.29.MirrorCS", {"start": v(-1419.15, 2300.15) * mm, "end": v(-1342.98, 2300.15) * mm});
            skLineSegment(sketch, "E204.30.MirrorCS", {"start": v(-258.9, 2300.15) * mm, "end": v(-335.07, 2300.15) * mm});
            skPoint(sketch, "E204.31.MirrorP", {"position": v(-360.47, 2300.15) * mm});
            skPoint(sketch, "E204.32.MirrorP", {"position": v(-233.5, 2300.15) * mm});
            skLineSegment(sketch, "E205.bottom", {"start": v(-1569.4, 2521.62) * mm, "end": v(1603.82, 2521.62) * mm});
            skLineSegment(sketch, "E205.top", {"start": v(-1569.4, 2242.6) * mm, "end": v(1603.82, 2242.6) * mm});
            skLineSegment(sketch, "E205.left", {"start": v(-1569.4, 2521.62) * mm, "end": v(-1569.4, 2242.6) * mm});
            skLineSegment(sketch, "E205.right", {"start": v(1603.82, 2521.62) * mm, "end": v(1603.82, 2242.6) * mm});
            skSolve(sketch);
        }
        {
            var Q0;
            {var subQ4=sQuery(id+"F30.wireOp",EDGE,"E187.bottom");Q0=makeQuery(id+"F30.imprint","IMPRINT",FACE,{"disambiguationData":[TD([[makeQuery(id+"F30.imprint","IMPRINT",EDGE,{"derivedFrom":subQ4}),-1.0]])]});}
            var Q1;
            {var subQ2=sQuery(id+"F30.wireOp",EDGE,"E204.14.MirrorCS");Q1=makeQuery(id+"F30.imprint","IMPRINT",FACE,{"disambiguationData":[TD([[makeQuery(id+"F30.imprint","IMPRINT",EDGE,{"derivedFrom":subQ2}),-1.0]])]});}
            var Q2;
            {var subQ3=sQuery(id+"F30.wireOp",EDGE,"E204.3.MirrorCS");Q2=makeQuery(id+"F30.imprint","IMPRINT",FACE,{"disambiguationData":[TD([[makeQuery(id+"F30.imprint","IMPRINT",EDGE,{"derivedFrom":subQ3}),1.0]])]});}
            var Q3;
            Q3=makeQuery(id+"F30.imprint","IMPRINT",FACE,{"disambiguationData":[TD([[makeQuery(id+"F30.imprint","IMPRINT",EDGE,{"derivedFrom":sQuery(id+"F30.wireOp",EDGE,"E187.left")}),-1.0]])]});
            var Q4;
            Q4=makeQuery(id+"F30.imprint","IMPRINT",FACE,{"disambiguationData":[TD([[makeQuery(id+"F30.imprint","IMPRINT",EDGE,{"derivedFrom":sQuery(id+"F30.wireOp",EDGE,"E187.right")}),1.0]])]});
            var Q5;
            Q5=makeQuery(id+"F30.imprint","IMPRINT",FACE,{"disambiguationData":[TD([[makeQuery(id+"F30.imprint","IMPRINT",EDGE,{"derivedFrom":sQuery(id+"F30.wireOp",EDGE,"E203.0.MirrorCS")}),1.0]])]});
            var Q6;
            Q6=makeQuery(id+"F30.imprint","IMPRINT",FACE,{"disambiguationData":[TD([[makeQuery(id+"F30.imprint","IMPRINT",EDGE,{"derivedFrom":sQuery(id+"F30.wireOp",EDGE,"E204.0.MirrorC")}),1.0]])]});
            var Q7;
            Q7=makeQuery(id+"F30.imprint","IMPRINT",FACE,{"disambiguationData":[TD([[makeQuery(id+"F30.imprint","IMPRINT",EDGE,{"derivedFrom":sQuery(id+"F30.wireOp",EDGE,"E204.4.MirrorC")}),1.0]])]});
            var Q8;
            Q8=makeQuery(id+"F30.imprint","IMPRINT",FACE,{"disambiguationData":[TD([[makeQuery(id+"F30.imprint","IMPRINT",EDGE,{"derivedFrom":sQuery(id+"F30.wireOp",EDGE,"E204.5.MirrorC")}),-1.0]])]});
            var Q9;
            Q9=makeQuery(id+"F30.imprint","IMPRINT",FACE,{"disambiguationData":[TD([[makeQuery(id+"F30.imprint","IMPRINT",EDGE,{"derivedFrom":sQuery(id+"F30.wireOp",EDGE,"E204.8.MirrorC")}),-1.0]])]});
            var Q10;
            Q10=makeQuery(id+"F30.imprint","IMPRINT",FACE,{"disambiguationData":[TD([[makeQuery(id+"F30.imprint","IMPRINT",EDGE,{"derivedFrom":sQuery(id+"F30.wireOp",EDGE,"E204.1.MirrorC")}),-1.0]])]});
            var Q11;
            Q11=makeQuery(id+"F30.imprint","IMPRINT",FACE,{"disambiguationData":[TD([[makeQuery(id+"F30.imprint","IMPRINT",EDGE,{"derivedFrom":sQuery(id+"F30.wireOp",EDGE,"E204.6.MirrorC")}),1.0]])]});
            var Q12;
            Q12=makeQuery(id+"F30.imprint","IMPRINT",FACE,{"disambiguationData":[TD([[makeQuery(id+"F30.imprint","IMPRINT",EDGE,{"derivedFrom":sQuery(id+"F30.wireOp",EDGE,"E204.7.MirrorC")}),-1.0]])]});
            var Q13;
            Q13=makeQuery(id+"F30.imprint","IMPRINT",FACE,{"disambiguationData":[TD([[makeQuery(id+"F30.imprint","IMPRINT",EDGE,{"derivedFrom":sQuery(id+"F30.wireOp",EDGE,"E204.10.MirrorC")}),1.0]])]});
            var Q14;
            Q14=makeQuery(id+"F30.imprint","IMPRINT",FACE,{"disambiguationData":[TD([[makeQuery(id+"F30.imprint","IMPRINT",EDGE,{"derivedFrom":sQuery(id+"F30.wireOp",EDGE,"E199.0.MirrorC")}),-1.0]])]});
            var Q15;
            Q15=makeQuery(id+"F30.imprint","IMPRINT",FACE,{"disambiguationData":[TD([[makeQuery(id+"F30.imprint","IMPRINT",EDGE,{"derivedFrom":sQuery(id+"F30.wireOp",EDGE,"E191")}),1.0]])]});
            var Q16;
            Q16=makeQuery(id+"F30.imprint","IMPRINT",FACE,{"disambiguationData":[TD([[makeQuery(id+"F30.imprint","IMPRINT",EDGE,{"derivedFrom":sQuery(id+"F30.wireOp",EDGE,"E193.0.MirrorC")}),-1.0]])]});
            var Q17;
            Q17=makeQuery(id+"F30.imprint","IMPRINT",FACE,{"disambiguationData":[TD([[makeQuery(id+"F30.imprint","IMPRINT",EDGE,{"derivedFrom":sQuery(id+"F30.wireOp",EDGE,"E198")}),1.0]])]});
            var Q18;
            Q18=makeQuery(id+"F30.imprint","IMPRINT",FACE,{"disambiguationData":[TD([[makeQuery(id+"F30.imprint","IMPRINT",EDGE,{"derivedFrom":sQuery(id+"F30.wireOp",EDGE,"E203.9.MirrorC")}),1.0]])]});
            var Q19;
            Q19=makeQuery(id+"F30.imprint","IMPRINT",FACE,{"disambiguationData":[TD([[makeQuery(id+"F30.imprint","IMPRINT",EDGE,{"derivedFrom":sQuery(id+"F30.wireOp",EDGE,"E203.8.MirrorC")}),-1.0]])]});
            var Q20;
            Q20=makeQuery(id+"F30.imprint","IMPRINT",FACE,{"disambiguationData":[TD([[makeQuery(id+"F30.imprint","IMPRINT",EDGE,{"derivedFrom":sQuery(id+"F30.wireOp",EDGE,"E203.11.MirrorC")}),-1.0]])]});
            var Q21;
            Q21=makeQuery(id+"F30.imprint","IMPRINT",FACE,{"disambiguationData":[TD([[makeQuery(id+"F30.imprint","IMPRINT",EDGE,{"derivedFrom":sQuery(id+"F30.wireOp",EDGE,"E203.10.MirrorC")}),1.0]])]});
            extrude(context, id + "F31", {"entities" : qUnion([Q0, Q1, Q2, Q3, Q4, Q5, Q6, Q7, Q8, Q9, Q10, Q11, Q12, Q13, Q14, Q15, Q16, Q17, Q18, Q19, Q20, Q21]), "operationType" : NewBodyOperationType.REMOVE, "oppositeDirection" : true, "depth" : 152.4 * mm});
        }
        {
            var Q0;
            Q0=makeQuery(id+"F30.imprint","IMPRINT",FACE,{"disambiguationData":[TD([[makeQuery(id+"F30.imprint","IMPRINT",EDGE,{"derivedFrom":sQuery(id+"F30.wireOp",EDGE,"E204.0.MirrorC")}),1.0]])]});
            var Q1;
            Q1=makeQuery(id+"F30.imprint","IMPRINT",FACE,{"disambiguationData":[TD([[makeQuery(id+"F30.imprint","IMPRINT",EDGE,{"derivedFrom":sQuery(id+"F30.wireOp",EDGE,"E204.8.MirrorC")}),-1.0]])]});
            var Q2;
            Q2=makeQuery(id+"F30.imprint","IMPRINT",FACE,{"disambiguationData":[TD([[makeQuery(id+"F30.imprint","IMPRINT",EDGE,{"derivedFrom":sQuery(id+"F30.wireOp",EDGE,"E204.1.MirrorC")}),-1.0]])]});
            var Q3;
            Q3=makeQuery(id+"F30.imprint","IMPRINT",FACE,{"disambiguationData":[TD([[makeQuery(id+"F30.imprint","IMPRINT",EDGE,{"derivedFrom":sQuery(id+"F30.wireOp",EDGE,"E204.10.MirrorC")}),1.0]])]});
            var Q4;
            Q4=makeQuery(id+"F30.imprint","IMPRINT",FACE,{"disambiguationData":[TD([[makeQuery(id+"F30.imprint","IMPRINT",EDGE,{"derivedFrom":sQuery(id+"F30.wireOp",EDGE,"E198")}),1.0]])]});
            var Q5;
            Q5=makeQuery(id+"F30.imprint","IMPRINT",FACE,{"disambiguationData":[TD([[makeQuery(id+"F30.imprint","IMPRINT",EDGE,{"derivedFrom":sQuery(id+"F30.wireOp",EDGE,"E199.0.MirrorC")}),-1.0]])]});
            var Q6;
            Q6=makeQuery(id+"F30.imprint","IMPRINT",FACE,{"disambiguationData":[TD([[makeQuery(id+"F30.imprint","IMPRINT",EDGE,{"derivedFrom":sQuery(id+"F30.wireOp",EDGE,"E203.11.MirrorC")}),-1.0]])]});
            var Q7;
            Q7=makeQuery(id+"F30.imprint","IMPRINT",FACE,{"disambiguationData":[TD([[makeQuery(id+"F30.imprint","IMPRINT",EDGE,{"derivedFrom":sQuery(id+"F30.wireOp",EDGE,"E203.10.MirrorC")}),1.0]])]});
            extrude(context, id + "F32", {"entities" : qUnion([Q0, Q1, Q2, Q3, Q4, Q5, Q6, Q7]), "operationType" : NewBodyOperationType.REMOVE, "depth" : 25.4 * mm});
        }
        {
            var Q0;
            Q0=makeQuery(id+"F30.imprint","IMPRINT",FACE,{"disambiguationData":[TD([[makeQuery(id+"F30.imprint","IMPRINT",EDGE,{"derivedFrom":sQuery(id+"F30.wireOp",EDGE,"E204.4.MirrorC")}),1.0]])]});
            var Q1;
            Q1=makeQuery(id+"F30.imprint","IMPRINT",FACE,{"disambiguationData":[TD([[makeQuery(id+"F30.imprint","IMPRINT",EDGE,{"derivedFrom":sQuery(id+"F30.wireOp",EDGE,"E204.5.MirrorC")}),-1.0]])]});
            var Q2;
            Q2=makeQuery(id+"F30.imprint","IMPRINT",FACE,{"disambiguationData":[TD([[makeQuery(id+"F30.imprint","IMPRINT",EDGE,{"derivedFrom":sQuery(id+"F30.wireOp",EDGE,"E204.6.MirrorC")}),1.0]])]});
            var Q3;
            Q3=makeQuery(id+"F30.imprint","IMPRINT",FACE,{"disambiguationData":[TD([[makeQuery(id+"F30.imprint","IMPRINT",EDGE,{"derivedFrom":sQuery(id+"F30.wireOp",EDGE,"E204.7.MirrorC")}),-1.0]])]});
            var Q4;
            Q4=makeQuery(id+"F30.imprint","IMPRINT",FACE,{"disambiguationData":[TD([[makeQuery(id+"F30.imprint","IMPRINT",EDGE,{"derivedFrom":sQuery(id+"F30.wireOp",EDGE,"E193.0.MirrorC")}),-1.0]])]});
            var Q5;
            Q5=makeQuery(id+"F30.imprint","IMPRINT",FACE,{"disambiguationData":[TD([[makeQuery(id+"F30.imprint","IMPRINT",EDGE,{"derivedFrom":sQuery(id+"F30.wireOp",EDGE,"E191")}),1.0]])]});
            var Q6;
            Q6=makeQuery(id+"F30.imprint","IMPRINT",FACE,{"disambiguationData":[TD([[makeQuery(id+"F30.imprint","IMPRINT",EDGE,{"derivedFrom":sQuery(id+"F30.wireOp",EDGE,"E203.9.MirrorC")}),1.0]])]});
            var Q7;
            Q7=makeQuery(id+"F30.imprint","IMPRINT",FACE,{"disambiguationData":[TD([[makeQuery(id+"F30.imprint","IMPRINT",EDGE,{"derivedFrom":sQuery(id+"F30.wireOp",EDGE,"E203.8.MirrorC")}),-1.0]])]});
            extrude(context, id + "F33", {"entities" : qUnion([Q0, Q1, Q2, Q3, Q4, Q5, Q6, Q7]), "operationType" : NewBodyOperationType.REMOVE, "oppositeDirection" : true, "depth" : 152.4 * mm});
        }
        {
            var Q0;
            Q0=qCreatedBy(makeId("Right.planeOp"),FACE);
            var sketch = newSketch(context, id + "F34", { "sketchPlane" : qUnion([Q0])});
            skLineSegment(sketch, "E206", {"start": v(-420.05, 3179.08) * mm, "end": v(-384.77, 3142.54) * mm});
            skLineSegment(sketch, "E207", {"start": v(-384.77, 3142.54) * mm, "end": v(-348.22, 3177.83) * mm});
            skLineSegment(sketch, "E208", {"start": v(-348.22, 3177.83) * mm, "end": v(-352.63, 3182.4) * mm});
            skLineSegment(sketch, "E209", {"start": v(-352.63, 3182.4) * mm, "end": v(-384.6, 3151.52) * mm});
            skLineSegment(sketch, "E210", {"start": v(-384.6, 3151.52) * mm, "end": v(-415.49, 3183.49) * mm});
            skLineSegment(sketch, "E211", {"start": v(-415.49, 3183.49) * mm, "end": v(-420.05, 3179.08) * mm});
            skLineSegment(sketch, "E212.0.MirrorCS", {"start": v(260, 3765.18) * mm, "end": v(255.6, 3769.75) * mm});
            skLineSegment(sketch, "E212.1.MirrorCS", {"start": v(256.69, 3832.6) * mm, "end": v(261.26, 3837.01) * mm});
            skLineSegment(sketch, "E212.2.MirrorCS", {"start": v(255.6, 3769.75) * mm, "end": v(287.57, 3800.63) * mm});
            skLineSegment(sketch, "E212.3.MirrorCS", {"start": v(287.57, 3800.63) * mm, "end": v(256.69, 3832.6) * mm});
            skLineSegment(sketch, "E212.4.MirrorCS", {"start": v(296.54, 3800.47) * mm, "end": v(260, 3765.18) * mm});
            skLineSegment(sketch, "E212.5.MirrorCS", {"start": v(261.26, 3837.01) * mm, "end": v(296.54, 3800.47) * mm});
            skSolve(sketch);
        }
        {
            var Q0;
            Q0 = qSketchRegion(id + "F34", true);
            var Q1;
            Q1=makeQuery(id+"F26.opExtrude","SWEPT_FACE",FACE,{"disambiguationData":[OSD([sQuery(id+"F25.wireOp",EDGE,"E155.0.MirrorCS")])]});
            var Q2;
            Q2=makeQuery(id+"F26.opExtrude","SWEPT_FACE",FACE,{"disambiguationData":[OSD([sQuery(id+"F25.wireOp",EDGE,"E154.3.MirrorCS")])]});
            extrude(context, id + "F35", {"entities" : qUnion([Q0]), "endBound" : BoundingType.UP_TO_SURFACE, "endBoundEntityFace" : qUnion([Q1]), "depth" : 25.4 * mm, "hasSecondDirection" : true, "secondDirectionBound" : SecondDirectionBoundingType.UP_TO_SURFACE, "secondDirectionOppositeDirection" : true, "secondDirectionBoundEntityFace" : qUnion([Q2]), "secondDirectionDepth" : 25.4 * mm});
        }
        {
            var Q0;
            Q0=makeQuery(id+"F29.opExtrude","SWEPT_FACE",FACE,{"disambiguationData":[OSD([sQuery(id+"F28.wireOp",EDGE,"E183.rect.left")])]});
            var sketch = newSketch(context, id + "F36", { "sketchPlane" : qUnion([Q0])});
            skCircle(sketch, "E213", {"center": v(0, 3106.99) * mm, "radius": 6.35 * mm});
            skLineSegment(sketch, "E214", {"start": v(50.8, 3106.99) * mm, "end": v(-50.8, 3106.99) * mm, "construction": true});
            skSolve(sketch);
        }
        {
            var Q0;
            Q0=sQuery(id+"F36.wireOp",EDGE,"E213");
            extrude(context, id + "F37", {"bodyType" : ToolBodyType.SURFACE, "surfaceEntities" : qUnion([Q0]), "depth" : 50.8 * mm, "hasSecondDirection" : true, "secondDirectionOppositeDirection" : true, "secondDirectionDepth" : 12.7 * mm});
        }
        {
            var Q0;
            Q0=makeQuery(id+"F29.opExtrude","SWEPT_FACE",FACE,{"disambiguationData":[OSD([sQuery(id+"F28.wireOp",EDGE,"E183.rect.left")])]});
            cPlane(context, id + "F38", {"entities" : qUnion([Q0]), "cplaneType" : CPlaneType.OFFSET, "offset" : 25.4 * mm, "width" : 152.4 * mm, "height" : 152.4 * mm});
        }
        {
            var Q0;
            Q0=qCreatedBy(id+"F38.planeOp",FACE);
            var sketch = newSketch(context, id + "F39", { "sketchPlane" : qUnion([Q0])});
            skCircle(sketch, "E215", {"center": v(-347.13, 3143.57) * mm, "radius": 6.35 * mm});
            skLineSegment(sketch, "E216", {"start": v(-347.13, 3143.57) * mm, "end": v(0, 3106.99) * mm, "construction": true});
            skLineSegment(sketch, "E217", {"start": v(-365.4, 3125.92) * mm, "end": v(-383.05, 3144.2) * mm});
            skLineSegment(sketch, "E218", {"start": v(-383.05, 3144.2) * mm, "end": v(-346.5, 3179.48) * mm});
            skLineSegment(sketch, "E219", {"start": v(-346.5, 3179.48) * mm, "end": v(-328.86, 3161.21) * mm});
            skArc(sketch, "E220", {"start": v(-365.4, 3125.92) * mm, "mid": v(-329.49, 3125.3) * mm, "end": v(-328.86, 3161.21) * mm});
            skLineSegment(sketch, "E221", {"start": v(-369.19, 3166.4) * mm, "end": v(-347.13, 3143.57) * mm, "construction": true});
            skLineSegment(sketch, "E222", {"start": v(-365.4, 3125.92) * mm, "end": v(-328.86, 3161.21) * mm, "construction": true});
            skLineSegment(sketch, "E223", {"start": v(-377.01, 3137.94) * mm, "end": v(-340.47, 3173.23) * mm});
            skSolve(sketch);
        }
        {
            var Q0;
            Q0=makeQuery(id+"F39.imprint","IMPRINT",FACE,{"disambiguationData":[TD([[makeQuery(id+"F39.imprint","IMPRINT",EDGE,{"derivedFrom":sQuery(id+"F39.wireOp",EDGE,"E215")}),-1.0]])]});
            var Q1;
            {var subQ2=sQuery(id+"F39.wireOp",EDGE,"E218");Q1=makeQuery(id+"F39.imprint","IMPRINT",FACE,{"disambiguationData":[TD([[makeQuery(id+"F39.imprint","IMPRINT",EDGE,{"derivedFrom":subQ2}),-1.0]])]});}
            extrude(context, id + "F40", {"entities" : qUnion([Q0, Q1]), "operationType" : NewBodyOperationType.ADD, "depth" : 6.35 * mm});
        }
        {
            var Q0;
            {var subQ2=sQuery(id+"F39.wireOp",EDGE,"E218");Q0=makeQuery(id+"F39.imprint","IMPRINT",FACE,{"disambiguationData":[TD([[makeQuery(id+"F39.imprint","IMPRINT",EDGE,{"derivedFrom":subQ2}),-1.0]])]});}
            extrude(context, id + "F41", {"entities" : qUnion([Q0]), "operationType" : NewBodyOperationType.ADD, "depth" : 25.4 * mm, "hasSecondDirection" : true, "secondDirectionOppositeDirection" : true, "secondDirectionDepth" : 25.4 * mm});
        }
        {
            var Q0;
            Q0=sQuery(id+"F39.wireOp",EDGE,"E216");
            var Q1;
            Q1=sQuery(id+"F39.wireOp",VERTEX,"E216.end");
            cPlane(context, id + "F42", {"entities" : qUnion([Q0, Q1]), "cplaneType" : CPlaneType.LINE_POINT, "offset" : 152.4 * mm, "width" : 152.4 * mm, "height" : 152.4 * mm});
        }
        {
            var Q0;
            Q0=qCreatedBy(id+"F42.planeOp",FACE);
            var sketch = newSketch(context, id + "F43", { "sketchPlane" : qUnion([Q0])});
            skCircle(sketch, "E224", {"center": v(-169.93, 3050.93) * mm, "radius": 25.4 * mm});
            skCircle(sketch, "E225", {"center": v(-169.93, 3050.93) * mm, "radius": 15.88 * mm});
            skSolve(sketch);
        }
        {
            var Q0;
            Q0=makeQuery(id+"F43.imprint","IMPRINT",FACE,{"disambiguationData":[TD([[makeQuery(id+"F43.imprint","IMPRINT",EDGE,{"derivedFrom":sQuery(id+"F43.wireOp",EDGE,"E224")}),1.0]])]});
            var Q1;
            Q1=makeQuery(id+"F43.imprint","IMPRINT",FACE,{"disambiguationData":[TD([[makeQuery(id+"F43.imprint","IMPRINT",EDGE,{"derivedFrom":sQuery(id+"F43.wireOp",EDGE,"E225")}),1.0]])]});
            extrude(context, id + "F44", {"entities" : qUnion([Q0, Q1]), "depth" : 685.8 * mm, "hasSecondDirection" : true, "secondDirectionOppositeDirection" : true, "secondDirectionDepth" : 76.2 * mm});
        }
        {
            var Q0;
            Q0=makeQuery(id+"F43.imprint","IMPRINT",FACE,{"disambiguationData":[TD([[makeQuery(id+"F43.imprint","IMPRINT",EDGE,{"derivedFrom":sQuery(id+"F43.wireOp",EDGE,"E225")}),1.0]])]});
            extrude(context, id + "F45", {"entities" : qUnion([Q0]), "operationType" : NewBodyOperationType.ADD, "oppositeDirection" : true, "depth" : 304.8 * mm});
        }
    });
